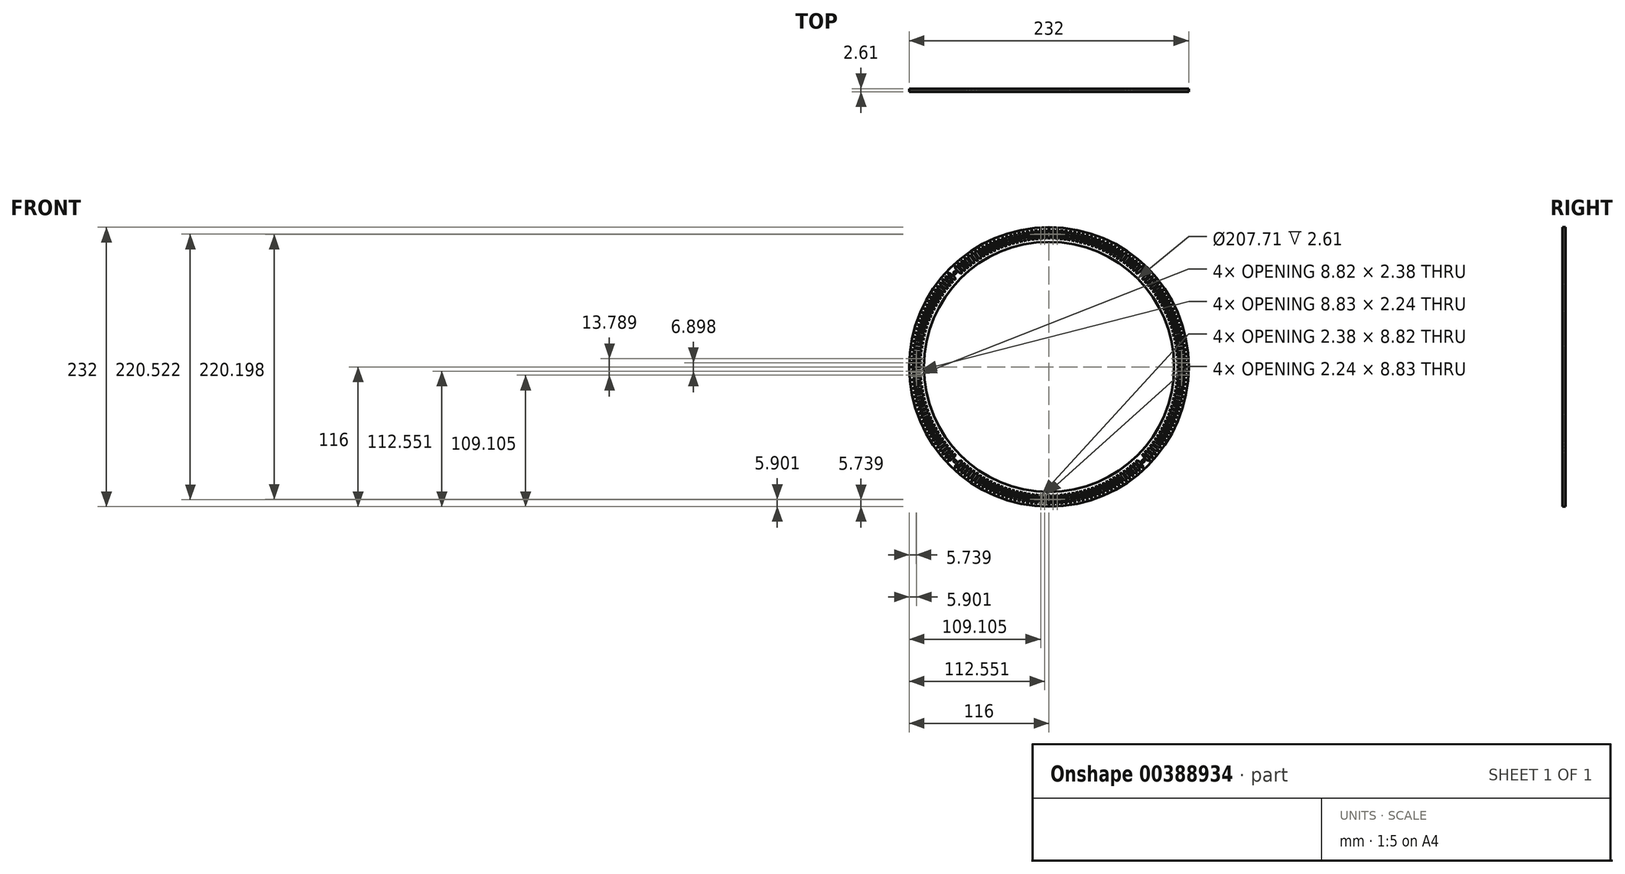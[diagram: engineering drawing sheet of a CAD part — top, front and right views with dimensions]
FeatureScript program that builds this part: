
annotation { "Feature Type Name" : "Feature", "Feature Type Description" : "" }
export const myFeature = defineFeature(function(context is Context, id is Id, definition is map)
    precondition{}
    {
        {
            var Q0;
            Q0=qCreatedBy(makeId("Front.planeOp"),FACE);
            var sketch = newSketch(context, id + "F0", { "sketchPlane" : qUnion([Q0])});
            skCircle(sketch, "E0", {"center": v(0, 0) * mm, "radius": 44.45 * mm});
            skCircle(sketch, "E1", {"center": v(0, 0) * mm, "radius": 39.8 * mm});
            skSolve(sketch);
        }
        {
            var Q0;
            Q0=makeQuery(id+"F0.imprint","IMPRINT",FACE,{"disambiguationData":[TD([[makeQuery(id+"F0.imprint","IMPRINT",EDGE,{"derivedFrom":sQuery(id+"F0.wireOp",EDGE,"E0")}),1.0]])]});
            extrude(context, id + "F1", {"entities" : qUnion([Q0]), "oppositeDirection" : true, "depth" : 1 * mm});
        }
        {
            var Q0;
            Q0=qCreatedBy(makeId("Front.planeOp"),FACE);
            var sketch = newSketch(context, id + "F2", { "sketchPlane" : qUnion([Q0])});
            skLineSegment(sketch, "E2", {"start": v(-43.11, 0.4) * mm, "end": v(-43.96, 0) * mm});
            skLineSegment(sketch, "E3", {"start": v(-41.42, 0.4) * mm, "end": v(-40.57, 0) * mm});
            skLineSegment(sketch, "E4", {"start": v(-40.57, 0) * mm, "end": v(-41.42, -0.4) * mm});
            skLineSegment(sketch, "E5", {"start": v(-43.96, 0) * mm, "end": v(-43.11, -0.4) * mm});
            skLineSegment(sketch, "E6", {"start": v(-43.11, 0.4) * mm, "end": v(-41.42, 0.4) * mm});
            skLineSegment(sketch, "E7", {"start": v(-41.42, -0.4) * mm, "end": v(-43.11, -0.4) * mm});
            skSolve(sketch);
        }
        {
            var Q0;
            Q0=qSketchRegion(id+"F2",true);
            extrude(context, id + "F3", {"entities" : qUnion([Q0]), "oppositeDirection" : true, "depth" : 1 * mm});
        }
        {
            var Q0;
            Q0=makeQuery(id+"F3.opExtrude","SWEPT_BODY",BODY,{"disambiguationData":[OSD([sQuery(id+"F2.wireOp",EDGE,"E2"),sQuery(id+"F2.wireOp",EDGE,"E3"),sQuery(id+"F2.wireOp",EDGE,"E4"),sQuery(id+"F2.wireOp",EDGE,"E5"),sQuery(id+"F2.wireOp",EDGE,"E6"),sQuery(id+"F2.wireOp",EDGE,"E7")])]});
            var Q1;
            Q1=sQuery(id+"F0.wireOp",EDGE,"E1");
            circularPattern(context, id + "F4", {"entities" : qUnion([Q0]), "axis" : qUnion([Q1]), "angle" : 43 * degree, "instanceCount" : 25, "equalSpace" : true});
        }
        {
            var Q0;
            Q0=makeQuery(id+"F3.opExtrude","SWEPT_BODY",BODY,{"disambiguationData":[OSD([sQuery(id+"F2.wireOp",EDGE,"E2"),sQuery(id+"F2.wireOp",EDGE,"E3"),sQuery(id+"F2.wireOp",EDGE,"E4"),sQuery(id+"F2.wireOp",EDGE,"E5"),sQuery(id+"F2.wireOp",EDGE,"E6"),sQuery(id+"F2.wireOp",EDGE,"E7")])]});
            var Q1;
            Q1=sQuery(id+"F0.wireOp",EDGE,"E1");
            circularPattern(context, id + "F5", {"entities" : qUnion([Q0]), "axis" : qUnion([Q1]), "angle" : 43 * degree, "instanceCount" : 25, "oppositeDirection" : true, "equalSpace" : true});
        }
        {
            var Q0;
            Q0=makeQuery(id+"F5.opPattern","COPY",BODY,{"derivedFrom":makeQuery(id+"F3.opExtrude","SWEPT_BODY",BODY,{"disambiguationData":[OSD([sQuery(id+"F2.wireOp",EDGE,"E2"),sQuery(id+"F2.wireOp",EDGE,"E3"),sQuery(id+"F2.wireOp",EDGE,"E4"),sQuery(id+"F2.wireOp",EDGE,"E5"),sQuery(id+"F2.wireOp",EDGE,"E6"),sQuery(id+"F2.wireOp",EDGE,"E7")])]}),"instanceName":"5"});
            var Q1;
            Q1=makeQuery(id+"F5.opPattern","COPY",BODY,{"derivedFrom":makeQuery(id+"F3.opExtrude","SWEPT_BODY",BODY,{"disambiguationData":[OSD([sQuery(id+"F2.wireOp",EDGE,"E2"),sQuery(id+"F2.wireOp",EDGE,"E3"),sQuery(id+"F2.wireOp",EDGE,"E4"),sQuery(id+"F2.wireOp",EDGE,"E5"),sQuery(id+"F2.wireOp",EDGE,"E6"),sQuery(id+"F2.wireOp",EDGE,"E7")])]}),"instanceName":"4"});
            var Q2;
            Q2=makeQuery(id+"F4.opPattern","COPY",BODY,{"derivedFrom":makeQuery(id+"F3.opExtrude","SWEPT_BODY",BODY,{"disambiguationData":[OSD([sQuery(id+"F2.wireOp",EDGE,"E2"),sQuery(id+"F2.wireOp",EDGE,"E3"),sQuery(id+"F2.wireOp",EDGE,"E4"),sQuery(id+"F2.wireOp",EDGE,"E5"),sQuery(id+"F2.wireOp",EDGE,"E6"),sQuery(id+"F2.wireOp",EDGE,"E7")])]}),"instanceName":"2"});
            var Q3;
            Q3=makeQuery(id+"F4.opPattern","COPY",BODY,{"derivedFrom":makeQuery(id+"F3.opExtrude","SWEPT_BODY",BODY,{"disambiguationData":[OSD([sQuery(id+"F2.wireOp",EDGE,"E2"),sQuery(id+"F2.wireOp",EDGE,"E3"),sQuery(id+"F2.wireOp",EDGE,"E4"),sQuery(id+"F2.wireOp",EDGE,"E5"),sQuery(id+"F2.wireOp",EDGE,"E6"),sQuery(id+"F2.wireOp",EDGE,"E7")])]}),"instanceName":"3"});
            var Q4;
            Q4=makeQuery(id+"F4.opPattern","COPY",BODY,{"derivedFrom":makeQuery(id+"F3.opExtrude","SWEPT_BODY",BODY,{"disambiguationData":[OSD([sQuery(id+"F2.wireOp",EDGE,"E2"),sQuery(id+"F2.wireOp",EDGE,"E3"),sQuery(id+"F2.wireOp",EDGE,"E4"),sQuery(id+"F2.wireOp",EDGE,"E5"),sQuery(id+"F2.wireOp",EDGE,"E6"),sQuery(id+"F2.wireOp",EDGE,"E7")])]}),"instanceName":"4"});
            var Q5;
            Q5=makeQuery(id+"F4.opPattern","COPY",BODY,{"derivedFrom":makeQuery(id+"F3.opExtrude","SWEPT_BODY",BODY,{"disambiguationData":[OSD([sQuery(id+"F2.wireOp",EDGE,"E2"),sQuery(id+"F2.wireOp",EDGE,"E3"),sQuery(id+"F2.wireOp",EDGE,"E4"),sQuery(id+"F2.wireOp",EDGE,"E5"),sQuery(id+"F2.wireOp",EDGE,"E6"),sQuery(id+"F2.wireOp",EDGE,"E7")])]}),"instanceName":"5"});
            var Q6;
            Q6=makeQuery(id+"F4.opPattern","COPY",BODY,{"derivedFrom":makeQuery(id+"F3.opExtrude","SWEPT_BODY",BODY,{"disambiguationData":[OSD([sQuery(id+"F2.wireOp",EDGE,"E2"),sQuery(id+"F2.wireOp",EDGE,"E3"),sQuery(id+"F2.wireOp",EDGE,"E4"),sQuery(id+"F2.wireOp",EDGE,"E5"),sQuery(id+"F2.wireOp",EDGE,"E6"),sQuery(id+"F2.wireOp",EDGE,"E7")])]}),"instanceName":"6"});
            var Q7;
            Q7=makeQuery(id+"F4.opPattern","COPY",BODY,{"derivedFrom":makeQuery(id+"F3.opExtrude","SWEPT_BODY",BODY,{"disambiguationData":[OSD([sQuery(id+"F2.wireOp",EDGE,"E2"),sQuery(id+"F2.wireOp",EDGE,"E3"),sQuery(id+"F2.wireOp",EDGE,"E4"),sQuery(id+"F2.wireOp",EDGE,"E5"),sQuery(id+"F2.wireOp",EDGE,"E6"),sQuery(id+"F2.wireOp",EDGE,"E7")])]}),"instanceName":"7"});
            var Q8;
            Q8=makeQuery(id+"F4.opPattern","COPY",BODY,{"derivedFrom":makeQuery(id+"F3.opExtrude","SWEPT_BODY",BODY,{"disambiguationData":[OSD([sQuery(id+"F2.wireOp",EDGE,"E2"),sQuery(id+"F2.wireOp",EDGE,"E3"),sQuery(id+"F2.wireOp",EDGE,"E4"),sQuery(id+"F2.wireOp",EDGE,"E5"),sQuery(id+"F2.wireOp",EDGE,"E6"),sQuery(id+"F2.wireOp",EDGE,"E7")])]}),"instanceName":"8"});
            var Q9;
            Q9=makeQuery(id+"F4.opPattern","COPY",BODY,{"derivedFrom":makeQuery(id+"F3.opExtrude","SWEPT_BODY",BODY,{"disambiguationData":[OSD([sQuery(id+"F2.wireOp",EDGE,"E2"),sQuery(id+"F2.wireOp",EDGE,"E3"),sQuery(id+"F2.wireOp",EDGE,"E4"),sQuery(id+"F2.wireOp",EDGE,"E5"),sQuery(id+"F2.wireOp",EDGE,"E6"),sQuery(id+"F2.wireOp",EDGE,"E7")])]}),"instanceName":"9"});
            var Q10;
            Q10=makeQuery(id+"F4.opPattern","COPY",BODY,{"derivedFrom":makeQuery(id+"F3.opExtrude","SWEPT_BODY",BODY,{"disambiguationData":[OSD([sQuery(id+"F2.wireOp",EDGE,"E2"),sQuery(id+"F2.wireOp",EDGE,"E3"),sQuery(id+"F2.wireOp",EDGE,"E4"),sQuery(id+"F2.wireOp",EDGE,"E5"),sQuery(id+"F2.wireOp",EDGE,"E6"),sQuery(id+"F2.wireOp",EDGE,"E7")])]}),"instanceName":"10"});
            var Q11;
            Q11=makeQuery(id+"F4.opPattern","COPY",BODY,{"derivedFrom":makeQuery(id+"F3.opExtrude","SWEPT_BODY",BODY,{"disambiguationData":[OSD([sQuery(id+"F2.wireOp",EDGE,"E2"),sQuery(id+"F2.wireOp",EDGE,"E3"),sQuery(id+"F2.wireOp",EDGE,"E4"),sQuery(id+"F2.wireOp",EDGE,"E5"),sQuery(id+"F2.wireOp",EDGE,"E6"),sQuery(id+"F2.wireOp",EDGE,"E7")])]}),"instanceName":"11"});
            var Q12;
            Q12=makeQuery(id+"F4.opPattern","COPY",BODY,{"derivedFrom":makeQuery(id+"F3.opExtrude","SWEPT_BODY",BODY,{"disambiguationData":[OSD([sQuery(id+"F2.wireOp",EDGE,"E2"),sQuery(id+"F2.wireOp",EDGE,"E3"),sQuery(id+"F2.wireOp",EDGE,"E4"),sQuery(id+"F2.wireOp",EDGE,"E5"),sQuery(id+"F2.wireOp",EDGE,"E6"),sQuery(id+"F2.wireOp",EDGE,"E7")])]}),"instanceName":"12"});
            var Q13;
            Q13=makeQuery(id+"F4.opPattern","COPY",BODY,{"derivedFrom":makeQuery(id+"F3.opExtrude","SWEPT_BODY",BODY,{"disambiguationData":[OSD([sQuery(id+"F2.wireOp",EDGE,"E2"),sQuery(id+"F2.wireOp",EDGE,"E3"),sQuery(id+"F2.wireOp",EDGE,"E4"),sQuery(id+"F2.wireOp",EDGE,"E5"),sQuery(id+"F2.wireOp",EDGE,"E6"),sQuery(id+"F2.wireOp",EDGE,"E7")])]}),"instanceName":"13"});
            var Q14;
            Q14=makeQuery(id+"F4.opPattern","COPY",BODY,{"derivedFrom":makeQuery(id+"F3.opExtrude","SWEPT_BODY",BODY,{"disambiguationData":[OSD([sQuery(id+"F2.wireOp",EDGE,"E2"),sQuery(id+"F2.wireOp",EDGE,"E3"),sQuery(id+"F2.wireOp",EDGE,"E4"),sQuery(id+"F2.wireOp",EDGE,"E5"),sQuery(id+"F2.wireOp",EDGE,"E6"),sQuery(id+"F2.wireOp",EDGE,"E7")])]}),"instanceName":"14"});
            var Q15;
            Q15=makeQuery(id+"F4.opPattern","COPY",BODY,{"derivedFrom":makeQuery(id+"F3.opExtrude","SWEPT_BODY",BODY,{"disambiguationData":[OSD([sQuery(id+"F2.wireOp",EDGE,"E2"),sQuery(id+"F2.wireOp",EDGE,"E3"),sQuery(id+"F2.wireOp",EDGE,"E4"),sQuery(id+"F2.wireOp",EDGE,"E5"),sQuery(id+"F2.wireOp",EDGE,"E6"),sQuery(id+"F2.wireOp",EDGE,"E7")])]}),"instanceName":"15"});
            var Q16;
            Q16=makeQuery(id+"F4.opPattern","COPY",BODY,{"derivedFrom":makeQuery(id+"F3.opExtrude","SWEPT_BODY",BODY,{"disambiguationData":[OSD([sQuery(id+"F2.wireOp",EDGE,"E2"),sQuery(id+"F2.wireOp",EDGE,"E3"),sQuery(id+"F2.wireOp",EDGE,"E4"),sQuery(id+"F2.wireOp",EDGE,"E5"),sQuery(id+"F2.wireOp",EDGE,"E6"),sQuery(id+"F2.wireOp",EDGE,"E7")])]}),"instanceName":"16"});
            var Q17;
            Q17=makeQuery(id+"F4.opPattern","COPY",BODY,{"derivedFrom":makeQuery(id+"F3.opExtrude","SWEPT_BODY",BODY,{"disambiguationData":[OSD([sQuery(id+"F2.wireOp",EDGE,"E2"),sQuery(id+"F2.wireOp",EDGE,"E3"),sQuery(id+"F2.wireOp",EDGE,"E4"),sQuery(id+"F2.wireOp",EDGE,"E5"),sQuery(id+"F2.wireOp",EDGE,"E6"),sQuery(id+"F2.wireOp",EDGE,"E7")])]}),"instanceName":"17"});
            var Q18;
            Q18=makeQuery(id+"F4.opPattern","COPY",BODY,{"derivedFrom":makeQuery(id+"F3.opExtrude","SWEPT_BODY",BODY,{"disambiguationData":[OSD([sQuery(id+"F2.wireOp",EDGE,"E2"),sQuery(id+"F2.wireOp",EDGE,"E3"),sQuery(id+"F2.wireOp",EDGE,"E4"),sQuery(id+"F2.wireOp",EDGE,"E5"),sQuery(id+"F2.wireOp",EDGE,"E6"),sQuery(id+"F2.wireOp",EDGE,"E7")])]}),"instanceName":"18"});
            var Q19;
            Q19=makeQuery(id+"F4.opPattern","COPY",BODY,{"derivedFrom":makeQuery(id+"F3.opExtrude","SWEPT_BODY",BODY,{"disambiguationData":[OSD([sQuery(id+"F2.wireOp",EDGE,"E2"),sQuery(id+"F2.wireOp",EDGE,"E3"),sQuery(id+"F2.wireOp",EDGE,"E4"),sQuery(id+"F2.wireOp",EDGE,"E5"),sQuery(id+"F2.wireOp",EDGE,"E6"),sQuery(id+"F2.wireOp",EDGE,"E7")])]}),"instanceName":"19"});
            var Q20;
            Q20=makeQuery(id+"F4.opPattern","COPY",BODY,{"derivedFrom":makeQuery(id+"F3.opExtrude","SWEPT_BODY",BODY,{"disambiguationData":[OSD([sQuery(id+"F2.wireOp",EDGE,"E2"),sQuery(id+"F2.wireOp",EDGE,"E3"),sQuery(id+"F2.wireOp",EDGE,"E4"),sQuery(id+"F2.wireOp",EDGE,"E5"),sQuery(id+"F2.wireOp",EDGE,"E6"),sQuery(id+"F2.wireOp",EDGE,"E7")])]}),"instanceName":"20"});
            var Q21;
            Q21=makeQuery(id+"F5.opPattern","COPY",BODY,{"derivedFrom":makeQuery(id+"F3.opExtrude","SWEPT_BODY",BODY,{"disambiguationData":[OSD([sQuery(id+"F2.wireOp",EDGE,"E2"),sQuery(id+"F2.wireOp",EDGE,"E3"),sQuery(id+"F2.wireOp",EDGE,"E4"),sQuery(id+"F2.wireOp",EDGE,"E5"),sQuery(id+"F2.wireOp",EDGE,"E6"),sQuery(id+"F2.wireOp",EDGE,"E7")])]}),"instanceName":"24"});
            var Q22;
            Q22=makeQuery(id+"F5.opPattern","COPY",BODY,{"derivedFrom":makeQuery(id+"F3.opExtrude","SWEPT_BODY",BODY,{"disambiguationData":[OSD([sQuery(id+"F2.wireOp",EDGE,"E2"),sQuery(id+"F2.wireOp",EDGE,"E3"),sQuery(id+"F2.wireOp",EDGE,"E4"),sQuery(id+"F2.wireOp",EDGE,"E5"),sQuery(id+"F2.wireOp",EDGE,"E6"),sQuery(id+"F2.wireOp",EDGE,"E7")])]}),"instanceName":"23"});
            var Q23;
            Q23=makeQuery(id+"F5.opPattern","COPY",BODY,{"derivedFrom":makeQuery(id+"F3.opExtrude","SWEPT_BODY",BODY,{"disambiguationData":[OSD([sQuery(id+"F2.wireOp",EDGE,"E2"),sQuery(id+"F2.wireOp",EDGE,"E3"),sQuery(id+"F2.wireOp",EDGE,"E4"),sQuery(id+"F2.wireOp",EDGE,"E5"),sQuery(id+"F2.wireOp",EDGE,"E6"),sQuery(id+"F2.wireOp",EDGE,"E7")])]}),"instanceName":"22"});
            var Q24;
            Q24=makeQuery(id+"F5.opPattern","COPY",BODY,{"derivedFrom":makeQuery(id+"F3.opExtrude","SWEPT_BODY",BODY,{"disambiguationData":[OSD([sQuery(id+"F2.wireOp",EDGE,"E2"),sQuery(id+"F2.wireOp",EDGE,"E3"),sQuery(id+"F2.wireOp",EDGE,"E4"),sQuery(id+"F2.wireOp",EDGE,"E5"),sQuery(id+"F2.wireOp",EDGE,"E6"),sQuery(id+"F2.wireOp",EDGE,"E7")])]}),"instanceName":"21"});
            var Q25;
            Q25=makeQuery(id+"F5.opPattern","COPY",BODY,{"derivedFrom":makeQuery(id+"F3.opExtrude","SWEPT_BODY",BODY,{"disambiguationData":[OSD([sQuery(id+"F2.wireOp",EDGE,"E2"),sQuery(id+"F2.wireOp",EDGE,"E3"),sQuery(id+"F2.wireOp",EDGE,"E4"),sQuery(id+"F2.wireOp",EDGE,"E5"),sQuery(id+"F2.wireOp",EDGE,"E6"),sQuery(id+"F2.wireOp",EDGE,"E7")])]}),"instanceName":"20"});
            var Q26;
            Q26=makeQuery(id+"F5.opPattern","COPY",BODY,{"derivedFrom":makeQuery(id+"F3.opExtrude","SWEPT_BODY",BODY,{"disambiguationData":[OSD([sQuery(id+"F2.wireOp",EDGE,"E2"),sQuery(id+"F2.wireOp",EDGE,"E3"),sQuery(id+"F2.wireOp",EDGE,"E4"),sQuery(id+"F2.wireOp",EDGE,"E5"),sQuery(id+"F2.wireOp",EDGE,"E6"),sQuery(id+"F2.wireOp",EDGE,"E7")])]}),"instanceName":"19"});
            var Q27;
            Q27=makeQuery(id+"F5.opPattern","COPY",BODY,{"derivedFrom":makeQuery(id+"F3.opExtrude","SWEPT_BODY",BODY,{"disambiguationData":[OSD([sQuery(id+"F2.wireOp",EDGE,"E2"),sQuery(id+"F2.wireOp",EDGE,"E3"),sQuery(id+"F2.wireOp",EDGE,"E4"),sQuery(id+"F2.wireOp",EDGE,"E5"),sQuery(id+"F2.wireOp",EDGE,"E6"),sQuery(id+"F2.wireOp",EDGE,"E7")])]}),"instanceName":"18"});
            var Q28;
            Q28=makeQuery(id+"F5.opPattern","COPY",BODY,{"derivedFrom":makeQuery(id+"F3.opExtrude","SWEPT_BODY",BODY,{"disambiguationData":[OSD([sQuery(id+"F2.wireOp",EDGE,"E2"),sQuery(id+"F2.wireOp",EDGE,"E3"),sQuery(id+"F2.wireOp",EDGE,"E4"),sQuery(id+"F2.wireOp",EDGE,"E5"),sQuery(id+"F2.wireOp",EDGE,"E6"),sQuery(id+"F2.wireOp",EDGE,"E7")])]}),"instanceName":"17"});
            var Q29;
            Q29=makeQuery(id+"F5.opPattern","COPY",BODY,{"derivedFrom":makeQuery(id+"F3.opExtrude","SWEPT_BODY",BODY,{"disambiguationData":[OSD([sQuery(id+"F2.wireOp",EDGE,"E2"),sQuery(id+"F2.wireOp",EDGE,"E3"),sQuery(id+"F2.wireOp",EDGE,"E4"),sQuery(id+"F2.wireOp",EDGE,"E5"),sQuery(id+"F2.wireOp",EDGE,"E6"),sQuery(id+"F2.wireOp",EDGE,"E7")])]}),"instanceName":"16"});
            var Q30;
            Q30=makeQuery(id+"F5.opPattern","COPY",BODY,{"derivedFrom":makeQuery(id+"F3.opExtrude","SWEPT_BODY",BODY,{"disambiguationData":[OSD([sQuery(id+"F2.wireOp",EDGE,"E2"),sQuery(id+"F2.wireOp",EDGE,"E3"),sQuery(id+"F2.wireOp",EDGE,"E4"),sQuery(id+"F2.wireOp",EDGE,"E5"),sQuery(id+"F2.wireOp",EDGE,"E6"),sQuery(id+"F2.wireOp",EDGE,"E7")])]}),"instanceName":"15"});
            var Q31;
            Q31=makeQuery(id+"F5.opPattern","COPY",BODY,{"derivedFrom":makeQuery(id+"F3.opExtrude","SWEPT_BODY",BODY,{"disambiguationData":[OSD([sQuery(id+"F2.wireOp",EDGE,"E2"),sQuery(id+"F2.wireOp",EDGE,"E3"),sQuery(id+"F2.wireOp",EDGE,"E4"),sQuery(id+"F2.wireOp",EDGE,"E5"),sQuery(id+"F2.wireOp",EDGE,"E6"),sQuery(id+"F2.wireOp",EDGE,"E7")])]}),"instanceName":"14"});
            var Q32;
            Q32=makeQuery(id+"F5.opPattern","COPY",BODY,{"derivedFrom":makeQuery(id+"F3.opExtrude","SWEPT_BODY",BODY,{"disambiguationData":[OSD([sQuery(id+"F2.wireOp",EDGE,"E2"),sQuery(id+"F2.wireOp",EDGE,"E3"),sQuery(id+"F2.wireOp",EDGE,"E4"),sQuery(id+"F2.wireOp",EDGE,"E5"),sQuery(id+"F2.wireOp",EDGE,"E6"),sQuery(id+"F2.wireOp",EDGE,"E7")])]}),"instanceName":"13"});
            var Q33;
            Q33=makeQuery(id+"F5.opPattern","COPY",BODY,{"derivedFrom":makeQuery(id+"F3.opExtrude","SWEPT_BODY",BODY,{"disambiguationData":[OSD([sQuery(id+"F2.wireOp",EDGE,"E2"),sQuery(id+"F2.wireOp",EDGE,"E3"),sQuery(id+"F2.wireOp",EDGE,"E4"),sQuery(id+"F2.wireOp",EDGE,"E5"),sQuery(id+"F2.wireOp",EDGE,"E6"),sQuery(id+"F2.wireOp",EDGE,"E7")])]}),"instanceName":"12"});
            var Q34;
            Q34=makeQuery(id+"F5.opPattern","COPY",BODY,{"derivedFrom":makeQuery(id+"F3.opExtrude","SWEPT_BODY",BODY,{"disambiguationData":[OSD([sQuery(id+"F2.wireOp",EDGE,"E2"),sQuery(id+"F2.wireOp",EDGE,"E3"),sQuery(id+"F2.wireOp",EDGE,"E4"),sQuery(id+"F2.wireOp",EDGE,"E5"),sQuery(id+"F2.wireOp",EDGE,"E6"),sQuery(id+"F2.wireOp",EDGE,"E7")])]}),"instanceName":"11"});
            var Q35;
            Q35=makeQuery(id+"F5.opPattern","COPY",BODY,{"derivedFrom":makeQuery(id+"F3.opExtrude","SWEPT_BODY",BODY,{"disambiguationData":[OSD([sQuery(id+"F2.wireOp",EDGE,"E2"),sQuery(id+"F2.wireOp",EDGE,"E3"),sQuery(id+"F2.wireOp",EDGE,"E4"),sQuery(id+"F2.wireOp",EDGE,"E5"),sQuery(id+"F2.wireOp",EDGE,"E6"),sQuery(id+"F2.wireOp",EDGE,"E7")])]}),"instanceName":"10"});
            var Q36;
            Q36=makeQuery(id+"F5.opPattern","COPY",BODY,{"derivedFrom":makeQuery(id+"F3.opExtrude","SWEPT_BODY",BODY,{"disambiguationData":[OSD([sQuery(id+"F2.wireOp",EDGE,"E2"),sQuery(id+"F2.wireOp",EDGE,"E3"),sQuery(id+"F2.wireOp",EDGE,"E4"),sQuery(id+"F2.wireOp",EDGE,"E5"),sQuery(id+"F2.wireOp",EDGE,"E6"),sQuery(id+"F2.wireOp",EDGE,"E7")])]}),"instanceName":"9"});
            var Q37;
            Q37=makeQuery(id+"F5.opPattern","COPY",BODY,{"derivedFrom":makeQuery(id+"F3.opExtrude","SWEPT_BODY",BODY,{"disambiguationData":[OSD([sQuery(id+"F2.wireOp",EDGE,"E2"),sQuery(id+"F2.wireOp",EDGE,"E3"),sQuery(id+"F2.wireOp",EDGE,"E4"),sQuery(id+"F2.wireOp",EDGE,"E5"),sQuery(id+"F2.wireOp",EDGE,"E6"),sQuery(id+"F2.wireOp",EDGE,"E7")])]}),"instanceName":"8"});
            var Q38;
            Q38=makeQuery(id+"F5.opPattern","COPY",BODY,{"derivedFrom":makeQuery(id+"F3.opExtrude","SWEPT_BODY",BODY,{"disambiguationData":[OSD([sQuery(id+"F2.wireOp",EDGE,"E2"),sQuery(id+"F2.wireOp",EDGE,"E3"),sQuery(id+"F2.wireOp",EDGE,"E4"),sQuery(id+"F2.wireOp",EDGE,"E5"),sQuery(id+"F2.wireOp",EDGE,"E6"),sQuery(id+"F2.wireOp",EDGE,"E7")])]}),"instanceName":"7"});
            var Q39;
            Q39=makeQuery(id+"F5.opPattern","COPY",BODY,{"derivedFrom":makeQuery(id+"F3.opExtrude","SWEPT_BODY",BODY,{"disambiguationData":[OSD([sQuery(id+"F2.wireOp",EDGE,"E2"),sQuery(id+"F2.wireOp",EDGE,"E3"),sQuery(id+"F2.wireOp",EDGE,"E4"),sQuery(id+"F2.wireOp",EDGE,"E5"),sQuery(id+"F2.wireOp",EDGE,"E6"),sQuery(id+"F2.wireOp",EDGE,"E7")])]}),"instanceName":"6"});
            var Q40;
            Q40=makeQuery(id+"F5.opPattern","COPY",BODY,{"derivedFrom":makeQuery(id+"F3.opExtrude","SWEPT_BODY",BODY,{"disambiguationData":[OSD([sQuery(id+"F2.wireOp",EDGE,"E2"),sQuery(id+"F2.wireOp",EDGE,"E3"),sQuery(id+"F2.wireOp",EDGE,"E4"),sQuery(id+"F2.wireOp",EDGE,"E5"),sQuery(id+"F2.wireOp",EDGE,"E6"),sQuery(id+"F2.wireOp",EDGE,"E7")])]}),"instanceName":"2"});
            var Q41;
            Q41=makeQuery(id+"F5.opPattern","COPY",BODY,{"derivedFrom":makeQuery(id+"F3.opExtrude","SWEPT_BODY",BODY,{"disambiguationData":[OSD([sQuery(id+"F2.wireOp",EDGE,"E2"),sQuery(id+"F2.wireOp",EDGE,"E3"),sQuery(id+"F2.wireOp",EDGE,"E4"),sQuery(id+"F2.wireOp",EDGE,"E5"),sQuery(id+"F2.wireOp",EDGE,"E6"),sQuery(id+"F2.wireOp",EDGE,"E7")])]}),"instanceName":"3"});
            var Q42;
            Q42=makeQuery(id+"F3.opExtrude","SWEPT_BODY",BODY,{"disambiguationData":[OSD([sQuery(id+"F2.wireOp",EDGE,"E2"),sQuery(id+"F2.wireOp",EDGE,"E3"),sQuery(id+"F2.wireOp",EDGE,"E4"),sQuery(id+"F2.wireOp",EDGE,"E5"),sQuery(id+"F2.wireOp",EDGE,"E6"),sQuery(id+"F2.wireOp",EDGE,"E7")])]});
            var Q43;
            Q43=makeQuery(id+"F4.opPattern","COPY",BODY,{"derivedFrom":makeQuery(id+"F3.opExtrude","SWEPT_BODY",BODY,{"disambiguationData":[OSD([sQuery(id+"F2.wireOp",EDGE,"E2"),sQuery(id+"F2.wireOp",EDGE,"E3"),sQuery(id+"F2.wireOp",EDGE,"E4"),sQuery(id+"F2.wireOp",EDGE,"E5"),sQuery(id+"F2.wireOp",EDGE,"E6"),sQuery(id+"F2.wireOp",EDGE,"E7")])]}),"instanceName":"1"});
            var Q44;
            Q44=makeQuery(id+"F5.opPattern","COPY",BODY,{"derivedFrom":makeQuery(id+"F3.opExtrude","SWEPT_BODY",BODY,{"disambiguationData":[OSD([sQuery(id+"F2.wireOp",EDGE,"E2"),sQuery(id+"F2.wireOp",EDGE,"E3"),sQuery(id+"F2.wireOp",EDGE,"E4"),sQuery(id+"F2.wireOp",EDGE,"E5"),sQuery(id+"F2.wireOp",EDGE,"E6"),sQuery(id+"F2.wireOp",EDGE,"E7")])]}),"instanceName":"1"});
            var Q45;
            Q45=makeQuery(id+"F4.opPattern","COPY",BODY,{"derivedFrom":makeQuery(id+"F3.opExtrude","SWEPT_BODY",BODY,{"disambiguationData":[OSD([sQuery(id+"F2.wireOp",EDGE,"E2"),sQuery(id+"F2.wireOp",EDGE,"E3"),sQuery(id+"F2.wireOp",EDGE,"E4"),sQuery(id+"F2.wireOp",EDGE,"E5"),sQuery(id+"F2.wireOp",EDGE,"E6"),sQuery(id+"F2.wireOp",EDGE,"E7")])]}),"instanceName":"21"});
            var Q46;
            Q46=makeQuery(id+"F4.opPattern","COPY",BODY,{"derivedFrom":makeQuery(id+"F3.opExtrude","SWEPT_BODY",BODY,{"disambiguationData":[OSD([sQuery(id+"F2.wireOp",EDGE,"E2"),sQuery(id+"F2.wireOp",EDGE,"E3"),sQuery(id+"F2.wireOp",EDGE,"E4"),sQuery(id+"F2.wireOp",EDGE,"E5"),sQuery(id+"F2.wireOp",EDGE,"E6"),sQuery(id+"F2.wireOp",EDGE,"E7")])]}),"instanceName":"22"});
            var Q47;
            Q47=makeQuery(id+"F4.opPattern","COPY",BODY,{"derivedFrom":makeQuery(id+"F3.opExtrude","SWEPT_BODY",BODY,{"disambiguationData":[OSD([sQuery(id+"F2.wireOp",EDGE,"E2"),sQuery(id+"F2.wireOp",EDGE,"E3"),sQuery(id+"F2.wireOp",EDGE,"E4"),sQuery(id+"F2.wireOp",EDGE,"E5"),sQuery(id+"F2.wireOp",EDGE,"E6"),sQuery(id+"F2.wireOp",EDGE,"E7")])]}),"instanceName":"23"});
            var Q48;
            Q48=makeQuery(id+"F4.opPattern","COPY",BODY,{"derivedFrom":makeQuery(id+"F3.opExtrude","SWEPT_BODY",BODY,{"disambiguationData":[OSD([sQuery(id+"F2.wireOp",EDGE,"E2"),sQuery(id+"F2.wireOp",EDGE,"E3"),sQuery(id+"F2.wireOp",EDGE,"E4"),sQuery(id+"F2.wireOp",EDGE,"E5"),sQuery(id+"F2.wireOp",EDGE,"E6"),sQuery(id+"F2.wireOp",EDGE,"E7")])]}),"instanceName":"24"});
            var Q49;
            Q49=sQuery(id+"F0.wireOp",EDGE,"E1");
            circularPattern(context, id + "F6", {"entities" : qUnion([Q0, Q1, Q2, Q3, Q4, Q5, Q6, Q7, Q8, Q9, Q10, Q11, Q12, Q13, Q14, Q15, Q16, Q17, Q18, Q19, Q20, Q21, Q22, Q23, Q24, Q25, Q26, Q27, Q28, Q29, Q30, Q31, Q32, Q33, Q34, Q35, Q36, Q37, Q38, Q39, Q40, Q41, Q42, Q43, Q44, Q45, Q46, Q47, Q48]), "axis" : qUnion([Q49]), "angle" : 360 * degree, "instanceCount" : 4, "equalSpace" : true});
        }
        {
            var Q0;
            Q0=makeQuery(id+"F0.imprint","IMPRINT",FACE,{"disambiguationData":[TD([[makeQuery(id+"F0.imprint","IMPRINT",EDGE,{"derivedFrom":sQuery(id+"F0.wireOp",EDGE,"E0")}),1.0]])]});
            var sketch = newSketch(context, id + "F7", { "sketchPlane" : qUnion([Q0])});
            skCircle(sketch, "E8", {"center": v(-29.95, -29.95) * mm, "radius": 0.45 * mm});
            skCircle(sketch, "E9.1.0", {"center": v(29.95, -29.95) * mm, "radius": 0.45 * mm});
            skCircle(sketch, "E9.2.0", {"center": v(29.95, 29.95) * mm, "radius": 0.45 * mm});
            skCircle(sketch, "E9.3.0", {"center": v(-29.95, 29.95) * mm, "radius": 0.45 * mm});
            skPoint(sketch, "E9.center", {"position": v(0, 0) * mm});
            skSolve(sketch);
        }
        {
            var Q0;
            Q0=qSketchRegion(id+"F7",true);
            extrude(context, id + "F8", {"entities" : qUnion([Q0]), "oppositeDirection" : true, "depth" : 1 * mm});
        }
        {
            var Q0;
            Q0=makeQuery(id+"F5.opPattern","COPY",BODY,{"derivedFrom":makeQuery(id+"F3.opExtrude","SWEPT_BODY",BODY,{"disambiguationData":[OSD([sQuery(id+"F2.wireOp",EDGE,"E2"),sQuery(id+"F2.wireOp",EDGE,"E3"),sQuery(id+"F2.wireOp",EDGE,"E4"),sQuery(id+"F2.wireOp",EDGE,"E5"),sQuery(id+"F2.wireOp",EDGE,"E6"),sQuery(id+"F2.wireOp",EDGE,"E7")])]}),"instanceName":"9"});
            var Q1;
            Q1=makeQuery(id+"F5.opPattern","COPY",BODY,{"derivedFrom":makeQuery(id+"F3.opExtrude","SWEPT_BODY",BODY,{"disambiguationData":[OSD([sQuery(id+"F2.wireOp",EDGE,"E2"),sQuery(id+"F2.wireOp",EDGE,"E3"),sQuery(id+"F2.wireOp",EDGE,"E4"),sQuery(id+"F2.wireOp",EDGE,"E5"),sQuery(id+"F2.wireOp",EDGE,"E6"),sQuery(id+"F2.wireOp",EDGE,"E7")])]}),"instanceName":"8"});
            var Q2;
            Q2=makeQuery(id+"F5.opPattern","COPY",BODY,{"derivedFrom":makeQuery(id+"F3.opExtrude","SWEPT_BODY",BODY,{"disambiguationData":[OSD([sQuery(id+"F2.wireOp",EDGE,"E2"),sQuery(id+"F2.wireOp",EDGE,"E3"),sQuery(id+"F2.wireOp",EDGE,"E4"),sQuery(id+"F2.wireOp",EDGE,"E5"),sQuery(id+"F2.wireOp",EDGE,"E6"),sQuery(id+"F2.wireOp",EDGE,"E7")])]}),"instanceName":"4"});
            var Q3;
            Q3=makeQuery(id+"F6.opPattern","COPY",BODY,{"derivedFrom":makeQuery(id+"F5.opPattern","COPY",BODY,{"derivedFrom":makeQuery(id+"F3.opExtrude","SWEPT_BODY",BODY,{"disambiguationData":[OSD([sQuery(id+"F2.wireOp",EDGE,"E2"),sQuery(id+"F2.wireOp",EDGE,"E3"),sQuery(id+"F2.wireOp",EDGE,"E4"),sQuery(id+"F2.wireOp",EDGE,"E5"),sQuery(id+"F2.wireOp",EDGE,"E6"),sQuery(id+"F2.wireOp",EDGE,"E7")])]}),"instanceName":"1"}),"instanceName":"3"});
            var Q4;
            Q4=makeQuery(id+"F6.opPattern","COPY",BODY,{"derivedFrom":makeQuery(id+"F5.opPattern","COPY",BODY,{"derivedFrom":makeQuery(id+"F3.opExtrude","SWEPT_BODY",BODY,{"disambiguationData":[OSD([sQuery(id+"F2.wireOp",EDGE,"E2"),sQuery(id+"F2.wireOp",EDGE,"E3"),sQuery(id+"F2.wireOp",EDGE,"E4"),sQuery(id+"F2.wireOp",EDGE,"E5"),sQuery(id+"F2.wireOp",EDGE,"E6"),sQuery(id+"F2.wireOp",EDGE,"E7")])]}),"instanceName":"23"}),"instanceName":"3"});
            var Q5;
            Q5=makeQuery(id+"F6.opPattern","COPY",BODY,{"derivedFrom":makeQuery(id+"F5.opPattern","COPY",BODY,{"derivedFrom":makeQuery(id+"F3.opExtrude","SWEPT_BODY",BODY,{"disambiguationData":[OSD([sQuery(id+"F2.wireOp",EDGE,"E2"),sQuery(id+"F2.wireOp",EDGE,"E3"),sQuery(id+"F2.wireOp",EDGE,"E4"),sQuery(id+"F2.wireOp",EDGE,"E5"),sQuery(id+"F2.wireOp",EDGE,"E6"),sQuery(id+"F2.wireOp",EDGE,"E7")])]}),"instanceName":"22"}),"instanceName":"3"});
            var Q6;
            Q6=makeQuery(id+"F6.opPattern","COPY",BODY,{"derivedFrom":makeQuery(id+"F5.opPattern","COPY",BODY,{"derivedFrom":makeQuery(id+"F3.opExtrude","SWEPT_BODY",BODY,{"disambiguationData":[OSD([sQuery(id+"F2.wireOp",EDGE,"E2"),sQuery(id+"F2.wireOp",EDGE,"E3"),sQuery(id+"F2.wireOp",EDGE,"E4"),sQuery(id+"F2.wireOp",EDGE,"E5"),sQuery(id+"F2.wireOp",EDGE,"E6"),sQuery(id+"F2.wireOp",EDGE,"E7")])]}),"instanceName":"21"}),"instanceName":"3"});
            var Q7;
            Q7=makeQuery(id+"F6.opPattern","COPY",BODY,{"derivedFrom":makeQuery(id+"F5.opPattern","COPY",BODY,{"derivedFrom":makeQuery(id+"F3.opExtrude","SWEPT_BODY",BODY,{"disambiguationData":[OSD([sQuery(id+"F2.wireOp",EDGE,"E2"),sQuery(id+"F2.wireOp",EDGE,"E3"),sQuery(id+"F2.wireOp",EDGE,"E4"),sQuery(id+"F2.wireOp",EDGE,"E5"),sQuery(id+"F2.wireOp",EDGE,"E6"),sQuery(id+"F2.wireOp",EDGE,"E7")])]}),"instanceName":"20"}),"instanceName":"3"});
            var Q8;
            Q8=makeQuery(id+"F6.opPattern","COPY",BODY,{"derivedFrom":makeQuery(id+"F5.opPattern","COPY",BODY,{"derivedFrom":makeQuery(id+"F3.opExtrude","SWEPT_BODY",BODY,{"disambiguationData":[OSD([sQuery(id+"F2.wireOp",EDGE,"E2"),sQuery(id+"F2.wireOp",EDGE,"E3"),sQuery(id+"F2.wireOp",EDGE,"E4"),sQuery(id+"F2.wireOp",EDGE,"E5"),sQuery(id+"F2.wireOp",EDGE,"E6"),sQuery(id+"F2.wireOp",EDGE,"E7")])]}),"instanceName":"19"}),"instanceName":"3"});
            var Q9;
            Q9=makeQuery(id+"F6.opPattern","COPY",BODY,{"derivedFrom":makeQuery(id+"F5.opPattern","COPY",BODY,{"derivedFrom":makeQuery(id+"F3.opExtrude","SWEPT_BODY",BODY,{"disambiguationData":[OSD([sQuery(id+"F2.wireOp",EDGE,"E2"),sQuery(id+"F2.wireOp",EDGE,"E3"),sQuery(id+"F2.wireOp",EDGE,"E4"),sQuery(id+"F2.wireOp",EDGE,"E5"),sQuery(id+"F2.wireOp",EDGE,"E6"),sQuery(id+"F2.wireOp",EDGE,"E7")])]}),"instanceName":"18"}),"instanceName":"3"});
            var Q10;
            Q10=makeQuery(id+"F6.opPattern","COPY",BODY,{"derivedFrom":makeQuery(id+"F5.opPattern","COPY",BODY,{"derivedFrom":makeQuery(id+"F3.opExtrude","SWEPT_BODY",BODY,{"disambiguationData":[OSD([sQuery(id+"F2.wireOp",EDGE,"E2"),sQuery(id+"F2.wireOp",EDGE,"E3"),sQuery(id+"F2.wireOp",EDGE,"E4"),sQuery(id+"F2.wireOp",EDGE,"E5"),sQuery(id+"F2.wireOp",EDGE,"E6"),sQuery(id+"F2.wireOp",EDGE,"E7")])]}),"instanceName":"17"}),"instanceName":"3"});
            var Q11;
            Q11=makeQuery(id+"F6.opPattern","COPY",BODY,{"derivedFrom":makeQuery(id+"F5.opPattern","COPY",BODY,{"derivedFrom":makeQuery(id+"F3.opExtrude","SWEPT_BODY",BODY,{"disambiguationData":[OSD([sQuery(id+"F2.wireOp",EDGE,"E2"),sQuery(id+"F2.wireOp",EDGE,"E3"),sQuery(id+"F2.wireOp",EDGE,"E4"),sQuery(id+"F2.wireOp",EDGE,"E5"),sQuery(id+"F2.wireOp",EDGE,"E6"),sQuery(id+"F2.wireOp",EDGE,"E7")])]}),"instanceName":"16"}),"instanceName":"3"});
            var Q12;
            Q12=makeQuery(id+"F6.opPattern","COPY",BODY,{"derivedFrom":makeQuery(id+"F5.opPattern","COPY",BODY,{"derivedFrom":makeQuery(id+"F3.opExtrude","SWEPT_BODY",BODY,{"disambiguationData":[OSD([sQuery(id+"F2.wireOp",EDGE,"E2"),sQuery(id+"F2.wireOp",EDGE,"E3"),sQuery(id+"F2.wireOp",EDGE,"E4"),sQuery(id+"F2.wireOp",EDGE,"E5"),sQuery(id+"F2.wireOp",EDGE,"E6"),sQuery(id+"F2.wireOp",EDGE,"E7")])]}),"instanceName":"15"}),"instanceName":"3"});
            var Q13;
            Q13=makeQuery(id+"F6.opPattern","COPY",BODY,{"derivedFrom":makeQuery(id+"F5.opPattern","COPY",BODY,{"derivedFrom":makeQuery(id+"F3.opExtrude","SWEPT_BODY",BODY,{"disambiguationData":[OSD([sQuery(id+"F2.wireOp",EDGE,"E2"),sQuery(id+"F2.wireOp",EDGE,"E3"),sQuery(id+"F2.wireOp",EDGE,"E4"),sQuery(id+"F2.wireOp",EDGE,"E5"),sQuery(id+"F2.wireOp",EDGE,"E6"),sQuery(id+"F2.wireOp",EDGE,"E7")])]}),"instanceName":"14"}),"instanceName":"3"});
            var Q14;
            Q14=makeQuery(id+"F6.opPattern","COPY",BODY,{"derivedFrom":makeQuery(id+"F5.opPattern","COPY",BODY,{"derivedFrom":makeQuery(id+"F3.opExtrude","SWEPT_BODY",BODY,{"disambiguationData":[OSD([sQuery(id+"F2.wireOp",EDGE,"E2"),sQuery(id+"F2.wireOp",EDGE,"E3"),sQuery(id+"F2.wireOp",EDGE,"E4"),sQuery(id+"F2.wireOp",EDGE,"E5"),sQuery(id+"F2.wireOp",EDGE,"E6"),sQuery(id+"F2.wireOp",EDGE,"E7")])]}),"instanceName":"13"}),"instanceName":"3"});
            var Q15;
            Q15=makeQuery(id+"F6.opPattern","COPY",BODY,{"derivedFrom":makeQuery(id+"F5.opPattern","COPY",BODY,{"derivedFrom":makeQuery(id+"F3.opExtrude","SWEPT_BODY",BODY,{"disambiguationData":[OSD([sQuery(id+"F2.wireOp",EDGE,"E2"),sQuery(id+"F2.wireOp",EDGE,"E3"),sQuery(id+"F2.wireOp",EDGE,"E4"),sQuery(id+"F2.wireOp",EDGE,"E5"),sQuery(id+"F2.wireOp",EDGE,"E6"),sQuery(id+"F2.wireOp",EDGE,"E7")])]}),"instanceName":"12"}),"instanceName":"3"});
            var Q16;
            Q16=makeQuery(id+"F6.opPattern","COPY",BODY,{"derivedFrom":makeQuery(id+"F5.opPattern","COPY",BODY,{"derivedFrom":makeQuery(id+"F3.opExtrude","SWEPT_BODY",BODY,{"disambiguationData":[OSD([sQuery(id+"F2.wireOp",EDGE,"E2"),sQuery(id+"F2.wireOp",EDGE,"E3"),sQuery(id+"F2.wireOp",EDGE,"E4"),sQuery(id+"F2.wireOp",EDGE,"E5"),sQuery(id+"F2.wireOp",EDGE,"E6"),sQuery(id+"F2.wireOp",EDGE,"E7")])]}),"instanceName":"11"}),"instanceName":"3"});
            var Q17;
            Q17=makeQuery(id+"F6.opPattern","COPY",BODY,{"derivedFrom":makeQuery(id+"F5.opPattern","COPY",BODY,{"derivedFrom":makeQuery(id+"F3.opExtrude","SWEPT_BODY",BODY,{"disambiguationData":[OSD([sQuery(id+"F2.wireOp",EDGE,"E2"),sQuery(id+"F2.wireOp",EDGE,"E3"),sQuery(id+"F2.wireOp",EDGE,"E4"),sQuery(id+"F2.wireOp",EDGE,"E5"),sQuery(id+"F2.wireOp",EDGE,"E6"),sQuery(id+"F2.wireOp",EDGE,"E7")])]}),"instanceName":"10"}),"instanceName":"3"});
            var Q18;
            Q18=makeQuery(id+"F6.opPattern","COPY",BODY,{"derivedFrom":makeQuery(id+"F5.opPattern","COPY",BODY,{"derivedFrom":makeQuery(id+"F3.opExtrude","SWEPT_BODY",BODY,{"disambiguationData":[OSD([sQuery(id+"F2.wireOp",EDGE,"E2"),sQuery(id+"F2.wireOp",EDGE,"E3"),sQuery(id+"F2.wireOp",EDGE,"E4"),sQuery(id+"F2.wireOp",EDGE,"E5"),sQuery(id+"F2.wireOp",EDGE,"E6"),sQuery(id+"F2.wireOp",EDGE,"E7")])]}),"instanceName":"9"}),"instanceName":"3"});
            var Q19;
            Q19=makeQuery(id+"F6.opPattern","COPY",BODY,{"derivedFrom":makeQuery(id+"F5.opPattern","COPY",BODY,{"derivedFrom":makeQuery(id+"F3.opExtrude","SWEPT_BODY",BODY,{"disambiguationData":[OSD([sQuery(id+"F2.wireOp",EDGE,"E2"),sQuery(id+"F2.wireOp",EDGE,"E3"),sQuery(id+"F2.wireOp",EDGE,"E4"),sQuery(id+"F2.wireOp",EDGE,"E5"),sQuery(id+"F2.wireOp",EDGE,"E6"),sQuery(id+"F2.wireOp",EDGE,"E7")])]}),"instanceName":"8"}),"instanceName":"3"});
            var Q20;
            Q20=makeQuery(id+"F6.opPattern","COPY",BODY,{"derivedFrom":makeQuery(id+"F5.opPattern","COPY",BODY,{"derivedFrom":makeQuery(id+"F3.opExtrude","SWEPT_BODY",BODY,{"disambiguationData":[OSD([sQuery(id+"F2.wireOp",EDGE,"E2"),sQuery(id+"F2.wireOp",EDGE,"E3"),sQuery(id+"F2.wireOp",EDGE,"E4"),sQuery(id+"F2.wireOp",EDGE,"E5"),sQuery(id+"F2.wireOp",EDGE,"E6"),sQuery(id+"F2.wireOp",EDGE,"E7")])]}),"instanceName":"7"}),"instanceName":"3"});
            var Q21;
            Q21=makeQuery(id+"F6.opPattern","COPY",BODY,{"derivedFrom":makeQuery(id+"F5.opPattern","COPY",BODY,{"derivedFrom":makeQuery(id+"F3.opExtrude","SWEPT_BODY",BODY,{"disambiguationData":[OSD([sQuery(id+"F2.wireOp",EDGE,"E2"),sQuery(id+"F2.wireOp",EDGE,"E3"),sQuery(id+"F2.wireOp",EDGE,"E4"),sQuery(id+"F2.wireOp",EDGE,"E5"),sQuery(id+"F2.wireOp",EDGE,"E6"),sQuery(id+"F2.wireOp",EDGE,"E7")])]}),"instanceName":"6"}),"instanceName":"3"});
            var Q22;
            Q22=makeQuery(id+"F6.opPattern","COPY",BODY,{"derivedFrom":makeQuery(id+"F5.opPattern","COPY",BODY,{"derivedFrom":makeQuery(id+"F3.opExtrude","SWEPT_BODY",BODY,{"disambiguationData":[OSD([sQuery(id+"F2.wireOp",EDGE,"E2"),sQuery(id+"F2.wireOp",EDGE,"E3"),sQuery(id+"F2.wireOp",EDGE,"E4"),sQuery(id+"F2.wireOp",EDGE,"E5"),sQuery(id+"F2.wireOp",EDGE,"E6"),sQuery(id+"F2.wireOp",EDGE,"E7")])]}),"instanceName":"5"}),"instanceName":"3"});
            var Q23;
            Q23=makeQuery(id+"F6.opPattern","COPY",BODY,{"derivedFrom":makeQuery(id+"F4.opPattern","COPY",BODY,{"derivedFrom":makeQuery(id+"F3.opExtrude","SWEPT_BODY",BODY,{"disambiguationData":[OSD([sQuery(id+"F2.wireOp",EDGE,"E2"),sQuery(id+"F2.wireOp",EDGE,"E3"),sQuery(id+"F2.wireOp",EDGE,"E4"),sQuery(id+"F2.wireOp",EDGE,"E5"),sQuery(id+"F2.wireOp",EDGE,"E6"),sQuery(id+"F2.wireOp",EDGE,"E7")])]}),"instanceName":"4"}),"instanceName":"1"});
            var Q24;
            Q24=makeQuery(id+"F6.opPattern","COPY",BODY,{"derivedFrom":makeQuery(id+"F4.opPattern","COPY",BODY,{"derivedFrom":makeQuery(id+"F3.opExtrude","SWEPT_BODY",BODY,{"disambiguationData":[OSD([sQuery(id+"F2.wireOp",EDGE,"E2"),sQuery(id+"F2.wireOp",EDGE,"E3"),sQuery(id+"F2.wireOp",EDGE,"E4"),sQuery(id+"F2.wireOp",EDGE,"E5"),sQuery(id+"F2.wireOp",EDGE,"E6"),sQuery(id+"F2.wireOp",EDGE,"E7")])]}),"instanceName":"5"}),"instanceName":"1"});
            var Q25;
            Q25=makeQuery(id+"F6.opPattern","COPY",BODY,{"derivedFrom":makeQuery(id+"F4.opPattern","COPY",BODY,{"derivedFrom":makeQuery(id+"F3.opExtrude","SWEPT_BODY",BODY,{"disambiguationData":[OSD([sQuery(id+"F2.wireOp",EDGE,"E2"),sQuery(id+"F2.wireOp",EDGE,"E3"),sQuery(id+"F2.wireOp",EDGE,"E4"),sQuery(id+"F2.wireOp",EDGE,"E5"),sQuery(id+"F2.wireOp",EDGE,"E6"),sQuery(id+"F2.wireOp",EDGE,"E7")])]}),"instanceName":"6"}),"instanceName":"1"});
            var Q26;
            Q26=makeQuery(id+"F6.opPattern","COPY",BODY,{"derivedFrom":makeQuery(id+"F4.opPattern","COPY",BODY,{"derivedFrom":makeQuery(id+"F3.opExtrude","SWEPT_BODY",BODY,{"disambiguationData":[OSD([sQuery(id+"F2.wireOp",EDGE,"E2"),sQuery(id+"F2.wireOp",EDGE,"E3"),sQuery(id+"F2.wireOp",EDGE,"E4"),sQuery(id+"F2.wireOp",EDGE,"E5"),sQuery(id+"F2.wireOp",EDGE,"E6"),sQuery(id+"F2.wireOp",EDGE,"E7")])]}),"instanceName":"7"}),"instanceName":"1"});
            var Q27;
            Q27=makeQuery(id+"F6.opPattern","COPY",BODY,{"derivedFrom":makeQuery(id+"F4.opPattern","COPY",BODY,{"derivedFrom":makeQuery(id+"F3.opExtrude","SWEPT_BODY",BODY,{"disambiguationData":[OSD([sQuery(id+"F2.wireOp",EDGE,"E2"),sQuery(id+"F2.wireOp",EDGE,"E3"),sQuery(id+"F2.wireOp",EDGE,"E4"),sQuery(id+"F2.wireOp",EDGE,"E5"),sQuery(id+"F2.wireOp",EDGE,"E6"),sQuery(id+"F2.wireOp",EDGE,"E7")])]}),"instanceName":"8"}),"instanceName":"1"});
            var Q28;
            Q28=makeQuery(id+"F6.opPattern","COPY",BODY,{"derivedFrom":makeQuery(id+"F4.opPattern","COPY",BODY,{"derivedFrom":makeQuery(id+"F3.opExtrude","SWEPT_BODY",BODY,{"disambiguationData":[OSD([sQuery(id+"F2.wireOp",EDGE,"E2"),sQuery(id+"F2.wireOp",EDGE,"E3"),sQuery(id+"F2.wireOp",EDGE,"E4"),sQuery(id+"F2.wireOp",EDGE,"E5"),sQuery(id+"F2.wireOp",EDGE,"E6"),sQuery(id+"F2.wireOp",EDGE,"E7")])]}),"instanceName":"9"}),"instanceName":"1"});
            var Q29;
            Q29=makeQuery(id+"F6.opPattern","COPY",BODY,{"derivedFrom":makeQuery(id+"F4.opPattern","COPY",BODY,{"derivedFrom":makeQuery(id+"F3.opExtrude","SWEPT_BODY",BODY,{"disambiguationData":[OSD([sQuery(id+"F2.wireOp",EDGE,"E2"),sQuery(id+"F2.wireOp",EDGE,"E3"),sQuery(id+"F2.wireOp",EDGE,"E4"),sQuery(id+"F2.wireOp",EDGE,"E5"),sQuery(id+"F2.wireOp",EDGE,"E6"),sQuery(id+"F2.wireOp",EDGE,"E7")])]}),"instanceName":"10"}),"instanceName":"1"});
            var Q30;
            Q30=makeQuery(id+"F6.opPattern","COPY",BODY,{"derivedFrom":makeQuery(id+"F4.opPattern","COPY",BODY,{"derivedFrom":makeQuery(id+"F3.opExtrude","SWEPT_BODY",BODY,{"disambiguationData":[OSD([sQuery(id+"F2.wireOp",EDGE,"E2"),sQuery(id+"F2.wireOp",EDGE,"E3"),sQuery(id+"F2.wireOp",EDGE,"E4"),sQuery(id+"F2.wireOp",EDGE,"E5"),sQuery(id+"F2.wireOp",EDGE,"E6"),sQuery(id+"F2.wireOp",EDGE,"E7")])]}),"instanceName":"11"}),"instanceName":"1"});
            var Q31;
            Q31=makeQuery(id+"F6.opPattern","COPY",BODY,{"derivedFrom":makeQuery(id+"F4.opPattern","COPY",BODY,{"derivedFrom":makeQuery(id+"F3.opExtrude","SWEPT_BODY",BODY,{"disambiguationData":[OSD([sQuery(id+"F2.wireOp",EDGE,"E2"),sQuery(id+"F2.wireOp",EDGE,"E3"),sQuery(id+"F2.wireOp",EDGE,"E4"),sQuery(id+"F2.wireOp",EDGE,"E5"),sQuery(id+"F2.wireOp",EDGE,"E6"),sQuery(id+"F2.wireOp",EDGE,"E7")])]}),"instanceName":"12"}),"instanceName":"1"});
            var Q32;
            Q32=makeQuery(id+"F6.opPattern","COPY",BODY,{"derivedFrom":makeQuery(id+"F4.opPattern","COPY",BODY,{"derivedFrom":makeQuery(id+"F3.opExtrude","SWEPT_BODY",BODY,{"disambiguationData":[OSD([sQuery(id+"F2.wireOp",EDGE,"E2"),sQuery(id+"F2.wireOp",EDGE,"E3"),sQuery(id+"F2.wireOp",EDGE,"E4"),sQuery(id+"F2.wireOp",EDGE,"E5"),sQuery(id+"F2.wireOp",EDGE,"E6"),sQuery(id+"F2.wireOp",EDGE,"E7")])]}),"instanceName":"13"}),"instanceName":"1"});
            var Q33;
            Q33=makeQuery(id+"F6.opPattern","COPY",BODY,{"derivedFrom":makeQuery(id+"F4.opPattern","COPY",BODY,{"derivedFrom":makeQuery(id+"F3.opExtrude","SWEPT_BODY",BODY,{"disambiguationData":[OSD([sQuery(id+"F2.wireOp",EDGE,"E2"),sQuery(id+"F2.wireOp",EDGE,"E3"),sQuery(id+"F2.wireOp",EDGE,"E4"),sQuery(id+"F2.wireOp",EDGE,"E5"),sQuery(id+"F2.wireOp",EDGE,"E6"),sQuery(id+"F2.wireOp",EDGE,"E7")])]}),"instanceName":"14"}),"instanceName":"1"});
            var Q34;
            Q34=makeQuery(id+"F6.opPattern","COPY",BODY,{"derivedFrom":makeQuery(id+"F4.opPattern","COPY",BODY,{"derivedFrom":makeQuery(id+"F3.opExtrude","SWEPT_BODY",BODY,{"disambiguationData":[OSD([sQuery(id+"F2.wireOp",EDGE,"E2"),sQuery(id+"F2.wireOp",EDGE,"E3"),sQuery(id+"F2.wireOp",EDGE,"E4"),sQuery(id+"F2.wireOp",EDGE,"E5"),sQuery(id+"F2.wireOp",EDGE,"E6"),sQuery(id+"F2.wireOp",EDGE,"E7")])]}),"instanceName":"15"}),"instanceName":"1"});
            var Q35;
            Q35=makeQuery(id+"F6.opPattern","COPY",BODY,{"derivedFrom":makeQuery(id+"F4.opPattern","COPY",BODY,{"derivedFrom":makeQuery(id+"F3.opExtrude","SWEPT_BODY",BODY,{"disambiguationData":[OSD([sQuery(id+"F2.wireOp",EDGE,"E2"),sQuery(id+"F2.wireOp",EDGE,"E3"),sQuery(id+"F2.wireOp",EDGE,"E4"),sQuery(id+"F2.wireOp",EDGE,"E5"),sQuery(id+"F2.wireOp",EDGE,"E6"),sQuery(id+"F2.wireOp",EDGE,"E7")])]}),"instanceName":"16"}),"instanceName":"1"});
            var Q36;
            Q36=makeQuery(id+"F6.opPattern","COPY",BODY,{"derivedFrom":makeQuery(id+"F4.opPattern","COPY",BODY,{"derivedFrom":makeQuery(id+"F3.opExtrude","SWEPT_BODY",BODY,{"disambiguationData":[OSD([sQuery(id+"F2.wireOp",EDGE,"E2"),sQuery(id+"F2.wireOp",EDGE,"E3"),sQuery(id+"F2.wireOp",EDGE,"E4"),sQuery(id+"F2.wireOp",EDGE,"E5"),sQuery(id+"F2.wireOp",EDGE,"E6"),sQuery(id+"F2.wireOp",EDGE,"E7")])]}),"instanceName":"17"}),"instanceName":"1"});
            var Q37;
            Q37=makeQuery(id+"F6.opPattern","COPY",BODY,{"derivedFrom":makeQuery(id+"F4.opPattern","COPY",BODY,{"derivedFrom":makeQuery(id+"F3.opExtrude","SWEPT_BODY",BODY,{"disambiguationData":[OSD([sQuery(id+"F2.wireOp",EDGE,"E2"),sQuery(id+"F2.wireOp",EDGE,"E3"),sQuery(id+"F2.wireOp",EDGE,"E4"),sQuery(id+"F2.wireOp",EDGE,"E5"),sQuery(id+"F2.wireOp",EDGE,"E6"),sQuery(id+"F2.wireOp",EDGE,"E7")])]}),"instanceName":"18"}),"instanceName":"1"});
            var Q38;
            Q38=makeQuery(id+"F6.opPattern","COPY",BODY,{"derivedFrom":makeQuery(id+"F4.opPattern","COPY",BODY,{"derivedFrom":makeQuery(id+"F3.opExtrude","SWEPT_BODY",BODY,{"disambiguationData":[OSD([sQuery(id+"F2.wireOp",EDGE,"E2"),sQuery(id+"F2.wireOp",EDGE,"E3"),sQuery(id+"F2.wireOp",EDGE,"E4"),sQuery(id+"F2.wireOp",EDGE,"E5"),sQuery(id+"F2.wireOp",EDGE,"E6"),sQuery(id+"F2.wireOp",EDGE,"E7")])]}),"instanceName":"19"}),"instanceName":"1"});
            var Q39;
            Q39=makeQuery(id+"F6.opPattern","COPY",BODY,{"derivedFrom":makeQuery(id+"F4.opPattern","COPY",BODY,{"derivedFrom":makeQuery(id+"F3.opExtrude","SWEPT_BODY",BODY,{"disambiguationData":[OSD([sQuery(id+"F2.wireOp",EDGE,"E2"),sQuery(id+"F2.wireOp",EDGE,"E3"),sQuery(id+"F2.wireOp",EDGE,"E4"),sQuery(id+"F2.wireOp",EDGE,"E5"),sQuery(id+"F2.wireOp",EDGE,"E6"),sQuery(id+"F2.wireOp",EDGE,"E7")])]}),"instanceName":"20"}),"instanceName":"1"});
            var Q40;
            Q40=makeQuery(id+"F6.opPattern","COPY",BODY,{"derivedFrom":makeQuery(id+"F4.opPattern","COPY",BODY,{"derivedFrom":makeQuery(id+"F3.opExtrude","SWEPT_BODY",BODY,{"disambiguationData":[OSD([sQuery(id+"F2.wireOp",EDGE,"E2"),sQuery(id+"F2.wireOp",EDGE,"E3"),sQuery(id+"F2.wireOp",EDGE,"E4"),sQuery(id+"F2.wireOp",EDGE,"E5"),sQuery(id+"F2.wireOp",EDGE,"E6"),sQuery(id+"F2.wireOp",EDGE,"E7")])]}),"instanceName":"21"}),"instanceName":"1"});
            var Q41;
            Q41=makeQuery(id+"F6.opPattern","COPY",BODY,{"derivedFrom":makeQuery(id+"F4.opPattern","COPY",BODY,{"derivedFrom":makeQuery(id+"F3.opExtrude","SWEPT_BODY",BODY,{"disambiguationData":[OSD([sQuery(id+"F2.wireOp",EDGE,"E2"),sQuery(id+"F2.wireOp",EDGE,"E3"),sQuery(id+"F2.wireOp",EDGE,"E4"),sQuery(id+"F2.wireOp",EDGE,"E5"),sQuery(id+"F2.wireOp",EDGE,"E6"),sQuery(id+"F2.wireOp",EDGE,"E7")])]}),"instanceName":"22"}),"instanceName":"1"});
            var Q42;
            Q42=makeQuery(id+"F6.opPattern","COPY",BODY,{"derivedFrom":makeQuery(id+"F4.opPattern","COPY",BODY,{"derivedFrom":makeQuery(id+"F3.opExtrude","SWEPT_BODY",BODY,{"disambiguationData":[OSD([sQuery(id+"F2.wireOp",EDGE,"E2"),sQuery(id+"F2.wireOp",EDGE,"E3"),sQuery(id+"F2.wireOp",EDGE,"E4"),sQuery(id+"F2.wireOp",EDGE,"E5"),sQuery(id+"F2.wireOp",EDGE,"E6"),sQuery(id+"F2.wireOp",EDGE,"E7")])]}),"instanceName":"23"}),"instanceName":"1"});
            var Q43;
            Q43=makeQuery(id+"F6.opPattern","COPY",BODY,{"derivedFrom":makeQuery(id+"F4.opPattern","COPY",BODY,{"derivedFrom":makeQuery(id+"F3.opExtrude","SWEPT_BODY",BODY,{"disambiguationData":[OSD([sQuery(id+"F2.wireOp",EDGE,"E2"),sQuery(id+"F2.wireOp",EDGE,"E3"),sQuery(id+"F2.wireOp",EDGE,"E4"),sQuery(id+"F2.wireOp",EDGE,"E5"),sQuery(id+"F2.wireOp",EDGE,"E6"),sQuery(id+"F2.wireOp",EDGE,"E7")])]}),"instanceName":"24"}),"instanceName":"1"});
            var Q44;
            Q44=makeQuery(id+"F6.opPattern","COPY",BODY,{"derivedFrom":makeQuery(id+"F5.opPattern","COPY",BODY,{"derivedFrom":makeQuery(id+"F3.opExtrude","SWEPT_BODY",BODY,{"disambiguationData":[OSD([sQuery(id+"F2.wireOp",EDGE,"E2"),sQuery(id+"F2.wireOp",EDGE,"E3"),sQuery(id+"F2.wireOp",EDGE,"E4"),sQuery(id+"F2.wireOp",EDGE,"E5"),sQuery(id+"F2.wireOp",EDGE,"E6"),sQuery(id+"F2.wireOp",EDGE,"E7")])]}),"instanceName":"1"}),"instanceName":"1"});
            var Q45;
            Q45=makeQuery(id+"F6.opPattern","COPY",BODY,{"derivedFrom":makeQuery(id+"F5.opPattern","COPY",BODY,{"derivedFrom":makeQuery(id+"F3.opExtrude","SWEPT_BODY",BODY,{"disambiguationData":[OSD([sQuery(id+"F2.wireOp",EDGE,"E2"),sQuery(id+"F2.wireOp",EDGE,"E3"),sQuery(id+"F2.wireOp",EDGE,"E4"),sQuery(id+"F2.wireOp",EDGE,"E5"),sQuery(id+"F2.wireOp",EDGE,"E6"),sQuery(id+"F2.wireOp",EDGE,"E7")])]}),"instanceName":"2"}),"instanceName":"1"});
            var Q46;
            Q46=makeQuery(id+"F6.opPattern","COPY",BODY,{"derivedFrom":makeQuery(id+"F5.opPattern","COPY",BODY,{"derivedFrom":makeQuery(id+"F3.opExtrude","SWEPT_BODY",BODY,{"disambiguationData":[OSD([sQuery(id+"F2.wireOp",EDGE,"E2"),sQuery(id+"F2.wireOp",EDGE,"E3"),sQuery(id+"F2.wireOp",EDGE,"E4"),sQuery(id+"F2.wireOp",EDGE,"E5"),sQuery(id+"F2.wireOp",EDGE,"E6"),sQuery(id+"F2.wireOp",EDGE,"E7")])]}),"instanceName":"3"}),"instanceName":"1"});
            var Q47;
            Q47=makeQuery(id+"F6.opPattern","COPY",BODY,{"derivedFrom":makeQuery(id+"F5.opPattern","COPY",BODY,{"derivedFrom":makeQuery(id+"F3.opExtrude","SWEPT_BODY",BODY,{"disambiguationData":[OSD([sQuery(id+"F2.wireOp",EDGE,"E2"),sQuery(id+"F2.wireOp",EDGE,"E3"),sQuery(id+"F2.wireOp",EDGE,"E4"),sQuery(id+"F2.wireOp",EDGE,"E5"),sQuery(id+"F2.wireOp",EDGE,"E6"),sQuery(id+"F2.wireOp",EDGE,"E7")])]}),"instanceName":"4"}),"instanceName":"1"});
            var Q48;
            Q48=makeQuery(id+"F6.opPattern","COPY",BODY,{"derivedFrom":makeQuery(id+"F5.opPattern","COPY",BODY,{"derivedFrom":makeQuery(id+"F3.opExtrude","SWEPT_BODY",BODY,{"disambiguationData":[OSD([sQuery(id+"F2.wireOp",EDGE,"E2"),sQuery(id+"F2.wireOp",EDGE,"E3"),sQuery(id+"F2.wireOp",EDGE,"E4"),sQuery(id+"F2.wireOp",EDGE,"E5"),sQuery(id+"F2.wireOp",EDGE,"E6"),sQuery(id+"F2.wireOp",EDGE,"E7")])]}),"instanceName":"5"}),"instanceName":"1"});
            var Q49;
            Q49=makeQuery(id+"F6.opPattern","COPY",BODY,{"derivedFrom":makeQuery(id+"F5.opPattern","COPY",BODY,{"derivedFrom":makeQuery(id+"F3.opExtrude","SWEPT_BODY",BODY,{"disambiguationData":[OSD([sQuery(id+"F2.wireOp",EDGE,"E2"),sQuery(id+"F2.wireOp",EDGE,"E3"),sQuery(id+"F2.wireOp",EDGE,"E4"),sQuery(id+"F2.wireOp",EDGE,"E5"),sQuery(id+"F2.wireOp",EDGE,"E6"),sQuery(id+"F2.wireOp",EDGE,"E7")])]}),"instanceName":"6"}),"instanceName":"1"});
            var Q50;
            Q50=makeQuery(id+"F6.opPattern","COPY",BODY,{"derivedFrom":makeQuery(id+"F5.opPattern","COPY",BODY,{"derivedFrom":makeQuery(id+"F3.opExtrude","SWEPT_BODY",BODY,{"disambiguationData":[OSD([sQuery(id+"F2.wireOp",EDGE,"E2"),sQuery(id+"F2.wireOp",EDGE,"E3"),sQuery(id+"F2.wireOp",EDGE,"E4"),sQuery(id+"F2.wireOp",EDGE,"E5"),sQuery(id+"F2.wireOp",EDGE,"E6"),sQuery(id+"F2.wireOp",EDGE,"E7")])]}),"instanceName":"7"}),"instanceName":"1"});
            var Q51;
            Q51=makeQuery(id+"F6.opPattern","COPY",BODY,{"derivedFrom":makeQuery(id+"F5.opPattern","COPY",BODY,{"derivedFrom":makeQuery(id+"F3.opExtrude","SWEPT_BODY",BODY,{"disambiguationData":[OSD([sQuery(id+"F2.wireOp",EDGE,"E2"),sQuery(id+"F2.wireOp",EDGE,"E3"),sQuery(id+"F2.wireOp",EDGE,"E4"),sQuery(id+"F2.wireOp",EDGE,"E5"),sQuery(id+"F2.wireOp",EDGE,"E6"),sQuery(id+"F2.wireOp",EDGE,"E7")])]}),"instanceName":"8"}),"instanceName":"1"});
            var Q52;
            Q52=makeQuery(id+"F6.opPattern","COPY",BODY,{"derivedFrom":makeQuery(id+"F5.opPattern","COPY",BODY,{"derivedFrom":makeQuery(id+"F3.opExtrude","SWEPT_BODY",BODY,{"disambiguationData":[OSD([sQuery(id+"F2.wireOp",EDGE,"E2"),sQuery(id+"F2.wireOp",EDGE,"E3"),sQuery(id+"F2.wireOp",EDGE,"E4"),sQuery(id+"F2.wireOp",EDGE,"E5"),sQuery(id+"F2.wireOp",EDGE,"E6"),sQuery(id+"F2.wireOp",EDGE,"E7")])]}),"instanceName":"9"}),"instanceName":"1"});
            var Q53;
            Q53=makeQuery(id+"F6.opPattern","COPY",BODY,{"derivedFrom":makeQuery(id+"F5.opPattern","COPY",BODY,{"derivedFrom":makeQuery(id+"F3.opExtrude","SWEPT_BODY",BODY,{"disambiguationData":[OSD([sQuery(id+"F2.wireOp",EDGE,"E2"),sQuery(id+"F2.wireOp",EDGE,"E3"),sQuery(id+"F2.wireOp",EDGE,"E4"),sQuery(id+"F2.wireOp",EDGE,"E5"),sQuery(id+"F2.wireOp",EDGE,"E6"),sQuery(id+"F2.wireOp",EDGE,"E7")])]}),"instanceName":"10"}),"instanceName":"1"});
            var Q54;
            Q54=makeQuery(id+"F6.opPattern","COPY",BODY,{"derivedFrom":makeQuery(id+"F5.opPattern","COPY",BODY,{"derivedFrom":makeQuery(id+"F3.opExtrude","SWEPT_BODY",BODY,{"disambiguationData":[OSD([sQuery(id+"F2.wireOp",EDGE,"E2"),sQuery(id+"F2.wireOp",EDGE,"E3"),sQuery(id+"F2.wireOp",EDGE,"E4"),sQuery(id+"F2.wireOp",EDGE,"E5"),sQuery(id+"F2.wireOp",EDGE,"E6"),sQuery(id+"F2.wireOp",EDGE,"E7")])]}),"instanceName":"11"}),"instanceName":"1"});
            var Q55;
            Q55=makeQuery(id+"F6.opPattern","COPY",BODY,{"derivedFrom":makeQuery(id+"F5.opPattern","COPY",BODY,{"derivedFrom":makeQuery(id+"F3.opExtrude","SWEPT_BODY",BODY,{"disambiguationData":[OSD([sQuery(id+"F2.wireOp",EDGE,"E2"),sQuery(id+"F2.wireOp",EDGE,"E3"),sQuery(id+"F2.wireOp",EDGE,"E4"),sQuery(id+"F2.wireOp",EDGE,"E5"),sQuery(id+"F2.wireOp",EDGE,"E6"),sQuery(id+"F2.wireOp",EDGE,"E7")])]}),"instanceName":"12"}),"instanceName":"1"});
            var Q56;
            Q56=makeQuery(id+"F6.opPattern","COPY",BODY,{"derivedFrom":makeQuery(id+"F5.opPattern","COPY",BODY,{"derivedFrom":makeQuery(id+"F3.opExtrude","SWEPT_BODY",BODY,{"disambiguationData":[OSD([sQuery(id+"F2.wireOp",EDGE,"E2"),sQuery(id+"F2.wireOp",EDGE,"E3"),sQuery(id+"F2.wireOp",EDGE,"E4"),sQuery(id+"F2.wireOp",EDGE,"E5"),sQuery(id+"F2.wireOp",EDGE,"E6"),sQuery(id+"F2.wireOp",EDGE,"E7")])]}),"instanceName":"13"}),"instanceName":"1"});
            var Q57;
            Q57=makeQuery(id+"F6.opPattern","COPY",BODY,{"derivedFrom":makeQuery(id+"F5.opPattern","COPY",BODY,{"derivedFrom":makeQuery(id+"F3.opExtrude","SWEPT_BODY",BODY,{"disambiguationData":[OSD([sQuery(id+"F2.wireOp",EDGE,"E2"),sQuery(id+"F2.wireOp",EDGE,"E3"),sQuery(id+"F2.wireOp",EDGE,"E4"),sQuery(id+"F2.wireOp",EDGE,"E5"),sQuery(id+"F2.wireOp",EDGE,"E6"),sQuery(id+"F2.wireOp",EDGE,"E7")])]}),"instanceName":"14"}),"instanceName":"1"});
            var Q58;
            Q58=makeQuery(id+"F6.opPattern","COPY",BODY,{"derivedFrom":makeQuery(id+"F5.opPattern","COPY",BODY,{"derivedFrom":makeQuery(id+"F3.opExtrude","SWEPT_BODY",BODY,{"disambiguationData":[OSD([sQuery(id+"F2.wireOp",EDGE,"E2"),sQuery(id+"F2.wireOp",EDGE,"E3"),sQuery(id+"F2.wireOp",EDGE,"E4"),sQuery(id+"F2.wireOp",EDGE,"E5"),sQuery(id+"F2.wireOp",EDGE,"E6"),sQuery(id+"F2.wireOp",EDGE,"E7")])]}),"instanceName":"15"}),"instanceName":"1"});
            var Q59;
            Q59=makeQuery(id+"F6.opPattern","COPY",BODY,{"derivedFrom":makeQuery(id+"F5.opPattern","COPY",BODY,{"derivedFrom":makeQuery(id+"F3.opExtrude","SWEPT_BODY",BODY,{"disambiguationData":[OSD([sQuery(id+"F2.wireOp",EDGE,"E2"),sQuery(id+"F2.wireOp",EDGE,"E3"),sQuery(id+"F2.wireOp",EDGE,"E4"),sQuery(id+"F2.wireOp",EDGE,"E5"),sQuery(id+"F2.wireOp",EDGE,"E6"),sQuery(id+"F2.wireOp",EDGE,"E7")])]}),"instanceName":"16"}),"instanceName":"1"});
            var Q60;
            Q60=makeQuery(id+"F6.opPattern","COPY",BODY,{"derivedFrom":makeQuery(id+"F5.opPattern","COPY",BODY,{"derivedFrom":makeQuery(id+"F3.opExtrude","SWEPT_BODY",BODY,{"disambiguationData":[OSD([sQuery(id+"F2.wireOp",EDGE,"E2"),sQuery(id+"F2.wireOp",EDGE,"E3"),sQuery(id+"F2.wireOp",EDGE,"E4"),sQuery(id+"F2.wireOp",EDGE,"E5"),sQuery(id+"F2.wireOp",EDGE,"E6"),sQuery(id+"F2.wireOp",EDGE,"E7")])]}),"instanceName":"17"}),"instanceName":"1"});
            var Q61;
            Q61=makeQuery(id+"F6.opPattern","COPY",BODY,{"derivedFrom":makeQuery(id+"F5.opPattern","COPY",BODY,{"derivedFrom":makeQuery(id+"F3.opExtrude","SWEPT_BODY",BODY,{"disambiguationData":[OSD([sQuery(id+"F2.wireOp",EDGE,"E2"),sQuery(id+"F2.wireOp",EDGE,"E3"),sQuery(id+"F2.wireOp",EDGE,"E4"),sQuery(id+"F2.wireOp",EDGE,"E5"),sQuery(id+"F2.wireOp",EDGE,"E6"),sQuery(id+"F2.wireOp",EDGE,"E7")])]}),"instanceName":"18"}),"instanceName":"1"});
            var Q62;
            Q62=makeQuery(id+"F6.opPattern","COPY",BODY,{"derivedFrom":makeQuery(id+"F5.opPattern","COPY",BODY,{"derivedFrom":makeQuery(id+"F3.opExtrude","SWEPT_BODY",BODY,{"disambiguationData":[OSD([sQuery(id+"F2.wireOp",EDGE,"E2"),sQuery(id+"F2.wireOp",EDGE,"E3"),sQuery(id+"F2.wireOp",EDGE,"E4"),sQuery(id+"F2.wireOp",EDGE,"E5"),sQuery(id+"F2.wireOp",EDGE,"E6"),sQuery(id+"F2.wireOp",EDGE,"E7")])]}),"instanceName":"19"}),"instanceName":"1"});
            var Q63;
            Q63=makeQuery(id+"F6.opPattern","COPY",BODY,{"derivedFrom":makeQuery(id+"F5.opPattern","COPY",BODY,{"derivedFrom":makeQuery(id+"F3.opExtrude","SWEPT_BODY",BODY,{"disambiguationData":[OSD([sQuery(id+"F2.wireOp",EDGE,"E2"),sQuery(id+"F2.wireOp",EDGE,"E3"),sQuery(id+"F2.wireOp",EDGE,"E4"),sQuery(id+"F2.wireOp",EDGE,"E5"),sQuery(id+"F2.wireOp",EDGE,"E6"),sQuery(id+"F2.wireOp",EDGE,"E7")])]}),"instanceName":"20"}),"instanceName":"1"});
            var Q64;
            Q64=makeQuery(id+"F6.opPattern","COPY",BODY,{"derivedFrom":makeQuery(id+"F5.opPattern","COPY",BODY,{"derivedFrom":makeQuery(id+"F3.opExtrude","SWEPT_BODY",BODY,{"disambiguationData":[OSD([sQuery(id+"F2.wireOp",EDGE,"E2"),sQuery(id+"F2.wireOp",EDGE,"E3"),sQuery(id+"F2.wireOp",EDGE,"E4"),sQuery(id+"F2.wireOp",EDGE,"E5"),sQuery(id+"F2.wireOp",EDGE,"E6"),sQuery(id+"F2.wireOp",EDGE,"E7")])]}),"instanceName":"21"}),"instanceName":"1"});
            var Q65;
            Q65=makeQuery(id+"F6.opPattern","COPY",BODY,{"derivedFrom":makeQuery(id+"F5.opPattern","COPY",BODY,{"derivedFrom":makeQuery(id+"F3.opExtrude","SWEPT_BODY",BODY,{"disambiguationData":[OSD([sQuery(id+"F2.wireOp",EDGE,"E2"),sQuery(id+"F2.wireOp",EDGE,"E3"),sQuery(id+"F2.wireOp",EDGE,"E4"),sQuery(id+"F2.wireOp",EDGE,"E5"),sQuery(id+"F2.wireOp",EDGE,"E6"),sQuery(id+"F2.wireOp",EDGE,"E7")])]}),"instanceName":"22"}),"instanceName":"1"});
            var Q66;
            Q66=makeQuery(id+"F6.opPattern","COPY",BODY,{"derivedFrom":makeQuery(id+"F5.opPattern","COPY",BODY,{"derivedFrom":makeQuery(id+"F3.opExtrude","SWEPT_BODY",BODY,{"disambiguationData":[OSD([sQuery(id+"F2.wireOp",EDGE,"E2"),sQuery(id+"F2.wireOp",EDGE,"E3"),sQuery(id+"F2.wireOp",EDGE,"E4"),sQuery(id+"F2.wireOp",EDGE,"E5"),sQuery(id+"F2.wireOp",EDGE,"E6"),sQuery(id+"F2.wireOp",EDGE,"E7")])]}),"instanceName":"23"}),"instanceName":"1"});
            var Q67;
            Q67=makeQuery(id+"F6.opPattern","COPY",BODY,{"derivedFrom":makeQuery(id+"F5.opPattern","COPY",BODY,{"derivedFrom":makeQuery(id+"F3.opExtrude","SWEPT_BODY",BODY,{"disambiguationData":[OSD([sQuery(id+"F2.wireOp",EDGE,"E2"),sQuery(id+"F2.wireOp",EDGE,"E3"),sQuery(id+"F2.wireOp",EDGE,"E4"),sQuery(id+"F2.wireOp",EDGE,"E5"),sQuery(id+"F2.wireOp",EDGE,"E6"),sQuery(id+"F2.wireOp",EDGE,"E7")])]}),"instanceName":"24"}),"instanceName":"1"});
            var Q68;
            Q68=makeQuery(id+"F6.opPattern","COPY",BODY,{"derivedFrom":makeQuery(id+"F3.opExtrude","SWEPT_BODY",BODY,{"disambiguationData":[OSD([sQuery(id+"F2.wireOp",EDGE,"E2"),sQuery(id+"F2.wireOp",EDGE,"E3"),sQuery(id+"F2.wireOp",EDGE,"E4"),sQuery(id+"F2.wireOp",EDGE,"E5"),sQuery(id+"F2.wireOp",EDGE,"E6"),sQuery(id+"F2.wireOp",EDGE,"E7")])]}),"instanceName":"2"});
            var Q69;
            Q69=makeQuery(id+"F6.opPattern","COPY",BODY,{"derivedFrom":makeQuery(id+"F4.opPattern","COPY",BODY,{"derivedFrom":makeQuery(id+"F3.opExtrude","SWEPT_BODY",BODY,{"disambiguationData":[OSD([sQuery(id+"F2.wireOp",EDGE,"E2"),sQuery(id+"F2.wireOp",EDGE,"E3"),sQuery(id+"F2.wireOp",EDGE,"E4"),sQuery(id+"F2.wireOp",EDGE,"E5"),sQuery(id+"F2.wireOp",EDGE,"E6"),sQuery(id+"F2.wireOp",EDGE,"E7")])]}),"instanceName":"1"}),"instanceName":"2"});
            var Q70;
            Q70=makeQuery(id+"F6.opPattern","COPY",BODY,{"derivedFrom":makeQuery(id+"F4.opPattern","COPY",BODY,{"derivedFrom":makeQuery(id+"F3.opExtrude","SWEPT_BODY",BODY,{"disambiguationData":[OSD([sQuery(id+"F2.wireOp",EDGE,"E2"),sQuery(id+"F2.wireOp",EDGE,"E3"),sQuery(id+"F2.wireOp",EDGE,"E4"),sQuery(id+"F2.wireOp",EDGE,"E5"),sQuery(id+"F2.wireOp",EDGE,"E6"),sQuery(id+"F2.wireOp",EDGE,"E7")])]}),"instanceName":"2"}),"instanceName":"2"});
            var Q71;
            Q71=makeQuery(id+"F6.opPattern","COPY",BODY,{"derivedFrom":makeQuery(id+"F4.opPattern","COPY",BODY,{"derivedFrom":makeQuery(id+"F3.opExtrude","SWEPT_BODY",BODY,{"disambiguationData":[OSD([sQuery(id+"F2.wireOp",EDGE,"E2"),sQuery(id+"F2.wireOp",EDGE,"E3"),sQuery(id+"F2.wireOp",EDGE,"E4"),sQuery(id+"F2.wireOp",EDGE,"E5"),sQuery(id+"F2.wireOp",EDGE,"E6"),sQuery(id+"F2.wireOp",EDGE,"E7")])]}),"instanceName":"3"}),"instanceName":"2"});
            var Q72;
            Q72=makeQuery(id+"F6.opPattern","COPY",BODY,{"derivedFrom":makeQuery(id+"F4.opPattern","COPY",BODY,{"derivedFrom":makeQuery(id+"F3.opExtrude","SWEPT_BODY",BODY,{"disambiguationData":[OSD([sQuery(id+"F2.wireOp",EDGE,"E2"),sQuery(id+"F2.wireOp",EDGE,"E3"),sQuery(id+"F2.wireOp",EDGE,"E4"),sQuery(id+"F2.wireOp",EDGE,"E5"),sQuery(id+"F2.wireOp",EDGE,"E6"),sQuery(id+"F2.wireOp",EDGE,"E7")])]}),"instanceName":"4"}),"instanceName":"2"});
            var Q73;
            Q73=makeQuery(id+"F6.opPattern","COPY",BODY,{"derivedFrom":makeQuery(id+"F4.opPattern","COPY",BODY,{"derivedFrom":makeQuery(id+"F3.opExtrude","SWEPT_BODY",BODY,{"disambiguationData":[OSD([sQuery(id+"F2.wireOp",EDGE,"E2"),sQuery(id+"F2.wireOp",EDGE,"E3"),sQuery(id+"F2.wireOp",EDGE,"E4"),sQuery(id+"F2.wireOp",EDGE,"E5"),sQuery(id+"F2.wireOp",EDGE,"E6"),sQuery(id+"F2.wireOp",EDGE,"E7")])]}),"instanceName":"5"}),"instanceName":"2"});
            var Q74;
            Q74=makeQuery(id+"F6.opPattern","COPY",BODY,{"derivedFrom":makeQuery(id+"F4.opPattern","COPY",BODY,{"derivedFrom":makeQuery(id+"F3.opExtrude","SWEPT_BODY",BODY,{"disambiguationData":[OSD([sQuery(id+"F2.wireOp",EDGE,"E2"),sQuery(id+"F2.wireOp",EDGE,"E3"),sQuery(id+"F2.wireOp",EDGE,"E4"),sQuery(id+"F2.wireOp",EDGE,"E5"),sQuery(id+"F2.wireOp",EDGE,"E6"),sQuery(id+"F2.wireOp",EDGE,"E7")])]}),"instanceName":"6"}),"instanceName":"2"});
            var Q75;
            Q75=makeQuery(id+"F6.opPattern","COPY",BODY,{"derivedFrom":makeQuery(id+"F4.opPattern","COPY",BODY,{"derivedFrom":makeQuery(id+"F3.opExtrude","SWEPT_BODY",BODY,{"disambiguationData":[OSD([sQuery(id+"F2.wireOp",EDGE,"E2"),sQuery(id+"F2.wireOp",EDGE,"E3"),sQuery(id+"F2.wireOp",EDGE,"E4"),sQuery(id+"F2.wireOp",EDGE,"E5"),sQuery(id+"F2.wireOp",EDGE,"E6"),sQuery(id+"F2.wireOp",EDGE,"E7")])]}),"instanceName":"7"}),"instanceName":"2"});
            var Q76;
            Q76=makeQuery(id+"F6.opPattern","COPY",BODY,{"derivedFrom":makeQuery(id+"F4.opPattern","COPY",BODY,{"derivedFrom":makeQuery(id+"F3.opExtrude","SWEPT_BODY",BODY,{"disambiguationData":[OSD([sQuery(id+"F2.wireOp",EDGE,"E2"),sQuery(id+"F2.wireOp",EDGE,"E3"),sQuery(id+"F2.wireOp",EDGE,"E4"),sQuery(id+"F2.wireOp",EDGE,"E5"),sQuery(id+"F2.wireOp",EDGE,"E6"),sQuery(id+"F2.wireOp",EDGE,"E7")])]}),"instanceName":"8"}),"instanceName":"2"});
            var Q77;
            Q77=makeQuery(id+"F6.opPattern","COPY",BODY,{"derivedFrom":makeQuery(id+"F4.opPattern","COPY",BODY,{"derivedFrom":makeQuery(id+"F3.opExtrude","SWEPT_BODY",BODY,{"disambiguationData":[OSD([sQuery(id+"F2.wireOp",EDGE,"E2"),sQuery(id+"F2.wireOp",EDGE,"E3"),sQuery(id+"F2.wireOp",EDGE,"E4"),sQuery(id+"F2.wireOp",EDGE,"E5"),sQuery(id+"F2.wireOp",EDGE,"E6"),sQuery(id+"F2.wireOp",EDGE,"E7")])]}),"instanceName":"9"}),"instanceName":"2"});
            var Q78;
            Q78=makeQuery(id+"F6.opPattern","COPY",BODY,{"derivedFrom":makeQuery(id+"F4.opPattern","COPY",BODY,{"derivedFrom":makeQuery(id+"F3.opExtrude","SWEPT_BODY",BODY,{"disambiguationData":[OSD([sQuery(id+"F2.wireOp",EDGE,"E2"),sQuery(id+"F2.wireOp",EDGE,"E3"),sQuery(id+"F2.wireOp",EDGE,"E4"),sQuery(id+"F2.wireOp",EDGE,"E5"),sQuery(id+"F2.wireOp",EDGE,"E6"),sQuery(id+"F2.wireOp",EDGE,"E7")])]}),"instanceName":"10"}),"instanceName":"2"});
            var Q79;
            Q79=makeQuery(id+"F6.opPattern","COPY",BODY,{"derivedFrom":makeQuery(id+"F4.opPattern","COPY",BODY,{"derivedFrom":makeQuery(id+"F3.opExtrude","SWEPT_BODY",BODY,{"disambiguationData":[OSD([sQuery(id+"F2.wireOp",EDGE,"E2"),sQuery(id+"F2.wireOp",EDGE,"E3"),sQuery(id+"F2.wireOp",EDGE,"E4"),sQuery(id+"F2.wireOp",EDGE,"E5"),sQuery(id+"F2.wireOp",EDGE,"E6"),sQuery(id+"F2.wireOp",EDGE,"E7")])]}),"instanceName":"11"}),"instanceName":"2"});
            var Q80;
            Q80=makeQuery(id+"F6.opPattern","COPY",BODY,{"derivedFrom":makeQuery(id+"F4.opPattern","COPY",BODY,{"derivedFrom":makeQuery(id+"F3.opExtrude","SWEPT_BODY",BODY,{"disambiguationData":[OSD([sQuery(id+"F2.wireOp",EDGE,"E2"),sQuery(id+"F2.wireOp",EDGE,"E3"),sQuery(id+"F2.wireOp",EDGE,"E4"),sQuery(id+"F2.wireOp",EDGE,"E5"),sQuery(id+"F2.wireOp",EDGE,"E6"),sQuery(id+"F2.wireOp",EDGE,"E7")])]}),"instanceName":"12"}),"instanceName":"2"});
            var Q81;
            Q81=makeQuery(id+"F6.opPattern","COPY",BODY,{"derivedFrom":makeQuery(id+"F4.opPattern","COPY",BODY,{"derivedFrom":makeQuery(id+"F3.opExtrude","SWEPT_BODY",BODY,{"disambiguationData":[OSD([sQuery(id+"F2.wireOp",EDGE,"E2"),sQuery(id+"F2.wireOp",EDGE,"E3"),sQuery(id+"F2.wireOp",EDGE,"E4"),sQuery(id+"F2.wireOp",EDGE,"E5"),sQuery(id+"F2.wireOp",EDGE,"E6"),sQuery(id+"F2.wireOp",EDGE,"E7")])]}),"instanceName":"13"}),"instanceName":"2"});
            var Q82;
            Q82=makeQuery(id+"F6.opPattern","COPY",BODY,{"derivedFrom":makeQuery(id+"F4.opPattern","COPY",BODY,{"derivedFrom":makeQuery(id+"F3.opExtrude","SWEPT_BODY",BODY,{"disambiguationData":[OSD([sQuery(id+"F2.wireOp",EDGE,"E2"),sQuery(id+"F2.wireOp",EDGE,"E3"),sQuery(id+"F2.wireOp",EDGE,"E4"),sQuery(id+"F2.wireOp",EDGE,"E5"),sQuery(id+"F2.wireOp",EDGE,"E6"),sQuery(id+"F2.wireOp",EDGE,"E7")])]}),"instanceName":"14"}),"instanceName":"2"});
            var Q83;
            Q83=makeQuery(id+"F6.opPattern","COPY",BODY,{"derivedFrom":makeQuery(id+"F4.opPattern","COPY",BODY,{"derivedFrom":makeQuery(id+"F3.opExtrude","SWEPT_BODY",BODY,{"disambiguationData":[OSD([sQuery(id+"F2.wireOp",EDGE,"E2"),sQuery(id+"F2.wireOp",EDGE,"E3"),sQuery(id+"F2.wireOp",EDGE,"E4"),sQuery(id+"F2.wireOp",EDGE,"E5"),sQuery(id+"F2.wireOp",EDGE,"E6"),sQuery(id+"F2.wireOp",EDGE,"E7")])]}),"instanceName":"15"}),"instanceName":"2"});
            var Q84;
            Q84=makeQuery(id+"F6.opPattern","COPY",BODY,{"derivedFrom":makeQuery(id+"F4.opPattern","COPY",BODY,{"derivedFrom":makeQuery(id+"F3.opExtrude","SWEPT_BODY",BODY,{"disambiguationData":[OSD([sQuery(id+"F2.wireOp",EDGE,"E2"),sQuery(id+"F2.wireOp",EDGE,"E3"),sQuery(id+"F2.wireOp",EDGE,"E4"),sQuery(id+"F2.wireOp",EDGE,"E5"),sQuery(id+"F2.wireOp",EDGE,"E6"),sQuery(id+"F2.wireOp",EDGE,"E7")])]}),"instanceName":"16"}),"instanceName":"2"});
            var Q85;
            Q85=makeQuery(id+"F6.opPattern","COPY",BODY,{"derivedFrom":makeQuery(id+"F4.opPattern","COPY",BODY,{"derivedFrom":makeQuery(id+"F3.opExtrude","SWEPT_BODY",BODY,{"disambiguationData":[OSD([sQuery(id+"F2.wireOp",EDGE,"E2"),sQuery(id+"F2.wireOp",EDGE,"E3"),sQuery(id+"F2.wireOp",EDGE,"E4"),sQuery(id+"F2.wireOp",EDGE,"E5"),sQuery(id+"F2.wireOp",EDGE,"E6"),sQuery(id+"F2.wireOp",EDGE,"E7")])]}),"instanceName":"17"}),"instanceName":"2"});
            var Q86;
            Q86=makeQuery(id+"F6.opPattern","COPY",BODY,{"derivedFrom":makeQuery(id+"F4.opPattern","COPY",BODY,{"derivedFrom":makeQuery(id+"F3.opExtrude","SWEPT_BODY",BODY,{"disambiguationData":[OSD([sQuery(id+"F2.wireOp",EDGE,"E2"),sQuery(id+"F2.wireOp",EDGE,"E3"),sQuery(id+"F2.wireOp",EDGE,"E4"),sQuery(id+"F2.wireOp",EDGE,"E5"),sQuery(id+"F2.wireOp",EDGE,"E6"),sQuery(id+"F2.wireOp",EDGE,"E7")])]}),"instanceName":"18"}),"instanceName":"2"});
            var Q87;
            Q87=makeQuery(id+"F6.opPattern","COPY",BODY,{"derivedFrom":makeQuery(id+"F4.opPattern","COPY",BODY,{"derivedFrom":makeQuery(id+"F3.opExtrude","SWEPT_BODY",BODY,{"disambiguationData":[OSD([sQuery(id+"F2.wireOp",EDGE,"E2"),sQuery(id+"F2.wireOp",EDGE,"E3"),sQuery(id+"F2.wireOp",EDGE,"E4"),sQuery(id+"F2.wireOp",EDGE,"E5"),sQuery(id+"F2.wireOp",EDGE,"E6"),sQuery(id+"F2.wireOp",EDGE,"E7")])]}),"instanceName":"19"}),"instanceName":"2"});
            var Q88;
            Q88=makeQuery(id+"F6.opPattern","COPY",BODY,{"derivedFrom":makeQuery(id+"F4.opPattern","COPY",BODY,{"derivedFrom":makeQuery(id+"F3.opExtrude","SWEPT_BODY",BODY,{"disambiguationData":[OSD([sQuery(id+"F2.wireOp",EDGE,"E2"),sQuery(id+"F2.wireOp",EDGE,"E3"),sQuery(id+"F2.wireOp",EDGE,"E4"),sQuery(id+"F2.wireOp",EDGE,"E5"),sQuery(id+"F2.wireOp",EDGE,"E6"),sQuery(id+"F2.wireOp",EDGE,"E7")])]}),"instanceName":"20"}),"instanceName":"2"});
            var Q89;
            Q89=makeQuery(id+"F6.opPattern","COPY",BODY,{"derivedFrom":makeQuery(id+"F4.opPattern","COPY",BODY,{"derivedFrom":makeQuery(id+"F3.opExtrude","SWEPT_BODY",BODY,{"disambiguationData":[OSD([sQuery(id+"F2.wireOp",EDGE,"E2"),sQuery(id+"F2.wireOp",EDGE,"E3"),sQuery(id+"F2.wireOp",EDGE,"E4"),sQuery(id+"F2.wireOp",EDGE,"E5"),sQuery(id+"F2.wireOp",EDGE,"E6"),sQuery(id+"F2.wireOp",EDGE,"E7")])]}),"instanceName":"21"}),"instanceName":"2"});
            var Q90;
            Q90=makeQuery(id+"F6.opPattern","COPY",BODY,{"derivedFrom":makeQuery(id+"F4.opPattern","COPY",BODY,{"derivedFrom":makeQuery(id+"F3.opExtrude","SWEPT_BODY",BODY,{"disambiguationData":[OSD([sQuery(id+"F2.wireOp",EDGE,"E2"),sQuery(id+"F2.wireOp",EDGE,"E3"),sQuery(id+"F2.wireOp",EDGE,"E4"),sQuery(id+"F2.wireOp",EDGE,"E5"),sQuery(id+"F2.wireOp",EDGE,"E6"),sQuery(id+"F2.wireOp",EDGE,"E7")])]}),"instanceName":"22"}),"instanceName":"2"});
            var Q91;
            Q91=makeQuery(id+"F6.opPattern","COPY",BODY,{"derivedFrom":makeQuery(id+"F4.opPattern","COPY",BODY,{"derivedFrom":makeQuery(id+"F3.opExtrude","SWEPT_BODY",BODY,{"disambiguationData":[OSD([sQuery(id+"F2.wireOp",EDGE,"E2"),sQuery(id+"F2.wireOp",EDGE,"E3"),sQuery(id+"F2.wireOp",EDGE,"E4"),sQuery(id+"F2.wireOp",EDGE,"E5"),sQuery(id+"F2.wireOp",EDGE,"E6"),sQuery(id+"F2.wireOp",EDGE,"E7")])]}),"instanceName":"23"}),"instanceName":"2"});
            var Q92;
            Q92=makeQuery(id+"F6.opPattern","COPY",BODY,{"derivedFrom":makeQuery(id+"F4.opPattern","COPY",BODY,{"derivedFrom":makeQuery(id+"F3.opExtrude","SWEPT_BODY",BODY,{"disambiguationData":[OSD([sQuery(id+"F2.wireOp",EDGE,"E2"),sQuery(id+"F2.wireOp",EDGE,"E3"),sQuery(id+"F2.wireOp",EDGE,"E4"),sQuery(id+"F2.wireOp",EDGE,"E5"),sQuery(id+"F2.wireOp",EDGE,"E6"),sQuery(id+"F2.wireOp",EDGE,"E7")])]}),"instanceName":"24"}),"instanceName":"2"});
            var Q93;
            Q93=makeQuery(id+"F6.opPattern","COPY",BODY,{"derivedFrom":makeQuery(id+"F5.opPattern","COPY",BODY,{"derivedFrom":makeQuery(id+"F3.opExtrude","SWEPT_BODY",BODY,{"disambiguationData":[OSD([sQuery(id+"F2.wireOp",EDGE,"E2"),sQuery(id+"F2.wireOp",EDGE,"E3"),sQuery(id+"F2.wireOp",EDGE,"E4"),sQuery(id+"F2.wireOp",EDGE,"E5"),sQuery(id+"F2.wireOp",EDGE,"E6"),sQuery(id+"F2.wireOp",EDGE,"E7")])]}),"instanceName":"1"}),"instanceName":"2"});
            var Q94;
            Q94=makeQuery(id+"F6.opPattern","COPY",BODY,{"derivedFrom":makeQuery(id+"F5.opPattern","COPY",BODY,{"derivedFrom":makeQuery(id+"F3.opExtrude","SWEPT_BODY",BODY,{"disambiguationData":[OSD([sQuery(id+"F2.wireOp",EDGE,"E2"),sQuery(id+"F2.wireOp",EDGE,"E3"),sQuery(id+"F2.wireOp",EDGE,"E4"),sQuery(id+"F2.wireOp",EDGE,"E5"),sQuery(id+"F2.wireOp",EDGE,"E6"),sQuery(id+"F2.wireOp",EDGE,"E7")])]}),"instanceName":"2"}),"instanceName":"2"});
            var Q95;
            Q95=makeQuery(id+"F6.opPattern","COPY",BODY,{"derivedFrom":makeQuery(id+"F5.opPattern","COPY",BODY,{"derivedFrom":makeQuery(id+"F3.opExtrude","SWEPT_BODY",BODY,{"disambiguationData":[OSD([sQuery(id+"F2.wireOp",EDGE,"E2"),sQuery(id+"F2.wireOp",EDGE,"E3"),sQuery(id+"F2.wireOp",EDGE,"E4"),sQuery(id+"F2.wireOp",EDGE,"E5"),sQuery(id+"F2.wireOp",EDGE,"E6"),sQuery(id+"F2.wireOp",EDGE,"E7")])]}),"instanceName":"3"}),"instanceName":"2"});
            var Q96;
            Q96=makeQuery(id+"F6.opPattern","COPY",BODY,{"derivedFrom":makeQuery(id+"F5.opPattern","COPY",BODY,{"derivedFrom":makeQuery(id+"F3.opExtrude","SWEPT_BODY",BODY,{"disambiguationData":[OSD([sQuery(id+"F2.wireOp",EDGE,"E2"),sQuery(id+"F2.wireOp",EDGE,"E3"),sQuery(id+"F2.wireOp",EDGE,"E4"),sQuery(id+"F2.wireOp",EDGE,"E5"),sQuery(id+"F2.wireOp",EDGE,"E6"),sQuery(id+"F2.wireOp",EDGE,"E7")])]}),"instanceName":"4"}),"instanceName":"2"});
            var Q97;
            Q97=makeQuery(id+"F6.opPattern","COPY",BODY,{"derivedFrom":makeQuery(id+"F5.opPattern","COPY",BODY,{"derivedFrom":makeQuery(id+"F3.opExtrude","SWEPT_BODY",BODY,{"disambiguationData":[OSD([sQuery(id+"F2.wireOp",EDGE,"E2"),sQuery(id+"F2.wireOp",EDGE,"E3"),sQuery(id+"F2.wireOp",EDGE,"E4"),sQuery(id+"F2.wireOp",EDGE,"E5"),sQuery(id+"F2.wireOp",EDGE,"E6"),sQuery(id+"F2.wireOp",EDGE,"E7")])]}),"instanceName":"5"}),"instanceName":"2"});
            var Q98;
            Q98=makeQuery(id+"F6.opPattern","COPY",BODY,{"derivedFrom":makeQuery(id+"F5.opPattern","COPY",BODY,{"derivedFrom":makeQuery(id+"F3.opExtrude","SWEPT_BODY",BODY,{"disambiguationData":[OSD([sQuery(id+"F2.wireOp",EDGE,"E2"),sQuery(id+"F2.wireOp",EDGE,"E3"),sQuery(id+"F2.wireOp",EDGE,"E4"),sQuery(id+"F2.wireOp",EDGE,"E5"),sQuery(id+"F2.wireOp",EDGE,"E6"),sQuery(id+"F2.wireOp",EDGE,"E7")])]}),"instanceName":"6"}),"instanceName":"2"});
            var Q99;
            Q99=makeQuery(id+"F6.opPattern","COPY",BODY,{"derivedFrom":makeQuery(id+"F5.opPattern","COPY",BODY,{"derivedFrom":makeQuery(id+"F3.opExtrude","SWEPT_BODY",BODY,{"disambiguationData":[OSD([sQuery(id+"F2.wireOp",EDGE,"E2"),sQuery(id+"F2.wireOp",EDGE,"E3"),sQuery(id+"F2.wireOp",EDGE,"E4"),sQuery(id+"F2.wireOp",EDGE,"E5"),sQuery(id+"F2.wireOp",EDGE,"E6"),sQuery(id+"F2.wireOp",EDGE,"E7")])]}),"instanceName":"7"}),"instanceName":"2"});
            var Q100;
            Q100=makeQuery(id+"F6.opPattern","COPY",BODY,{"derivedFrom":makeQuery(id+"F5.opPattern","COPY",BODY,{"derivedFrom":makeQuery(id+"F3.opExtrude","SWEPT_BODY",BODY,{"disambiguationData":[OSD([sQuery(id+"F2.wireOp",EDGE,"E2"),sQuery(id+"F2.wireOp",EDGE,"E3"),sQuery(id+"F2.wireOp",EDGE,"E4"),sQuery(id+"F2.wireOp",EDGE,"E5"),sQuery(id+"F2.wireOp",EDGE,"E6"),sQuery(id+"F2.wireOp",EDGE,"E7")])]}),"instanceName":"8"}),"instanceName":"2"});
            var Q101;
            Q101=makeQuery(id+"F6.opPattern","COPY",BODY,{"derivedFrom":makeQuery(id+"F5.opPattern","COPY",BODY,{"derivedFrom":makeQuery(id+"F3.opExtrude","SWEPT_BODY",BODY,{"disambiguationData":[OSD([sQuery(id+"F2.wireOp",EDGE,"E2"),sQuery(id+"F2.wireOp",EDGE,"E3"),sQuery(id+"F2.wireOp",EDGE,"E4"),sQuery(id+"F2.wireOp",EDGE,"E5"),sQuery(id+"F2.wireOp",EDGE,"E6"),sQuery(id+"F2.wireOp",EDGE,"E7")])]}),"instanceName":"9"}),"instanceName":"2"});
            var Q102;
            Q102=makeQuery(id+"F6.opPattern","COPY",BODY,{"derivedFrom":makeQuery(id+"F5.opPattern","COPY",BODY,{"derivedFrom":makeQuery(id+"F3.opExtrude","SWEPT_BODY",BODY,{"disambiguationData":[OSD([sQuery(id+"F2.wireOp",EDGE,"E2"),sQuery(id+"F2.wireOp",EDGE,"E3"),sQuery(id+"F2.wireOp",EDGE,"E4"),sQuery(id+"F2.wireOp",EDGE,"E5"),sQuery(id+"F2.wireOp",EDGE,"E6"),sQuery(id+"F2.wireOp",EDGE,"E7")])]}),"instanceName":"10"}),"instanceName":"2"});
            var Q103;
            Q103=makeQuery(id+"F6.opPattern","COPY",BODY,{"derivedFrom":makeQuery(id+"F5.opPattern","COPY",BODY,{"derivedFrom":makeQuery(id+"F3.opExtrude","SWEPT_BODY",BODY,{"disambiguationData":[OSD([sQuery(id+"F2.wireOp",EDGE,"E2"),sQuery(id+"F2.wireOp",EDGE,"E3"),sQuery(id+"F2.wireOp",EDGE,"E4"),sQuery(id+"F2.wireOp",EDGE,"E5"),sQuery(id+"F2.wireOp",EDGE,"E6"),sQuery(id+"F2.wireOp",EDGE,"E7")])]}),"instanceName":"11"}),"instanceName":"2"});
            var Q104;
            Q104=makeQuery(id+"F6.opPattern","COPY",BODY,{"derivedFrom":makeQuery(id+"F5.opPattern","COPY",BODY,{"derivedFrom":makeQuery(id+"F3.opExtrude","SWEPT_BODY",BODY,{"disambiguationData":[OSD([sQuery(id+"F2.wireOp",EDGE,"E2"),sQuery(id+"F2.wireOp",EDGE,"E3"),sQuery(id+"F2.wireOp",EDGE,"E4"),sQuery(id+"F2.wireOp",EDGE,"E5"),sQuery(id+"F2.wireOp",EDGE,"E6"),sQuery(id+"F2.wireOp",EDGE,"E7")])]}),"instanceName":"12"}),"instanceName":"2"});
            var Q105;
            Q105=makeQuery(id+"F6.opPattern","COPY",BODY,{"derivedFrom":makeQuery(id+"F5.opPattern","COPY",BODY,{"derivedFrom":makeQuery(id+"F3.opExtrude","SWEPT_BODY",BODY,{"disambiguationData":[OSD([sQuery(id+"F2.wireOp",EDGE,"E2"),sQuery(id+"F2.wireOp",EDGE,"E3"),sQuery(id+"F2.wireOp",EDGE,"E4"),sQuery(id+"F2.wireOp",EDGE,"E5"),sQuery(id+"F2.wireOp",EDGE,"E6"),sQuery(id+"F2.wireOp",EDGE,"E7")])]}),"instanceName":"13"}),"instanceName":"2"});
            var Q106;
            Q106=makeQuery(id+"F6.opPattern","COPY",BODY,{"derivedFrom":makeQuery(id+"F5.opPattern","COPY",BODY,{"derivedFrom":makeQuery(id+"F3.opExtrude","SWEPT_BODY",BODY,{"disambiguationData":[OSD([sQuery(id+"F2.wireOp",EDGE,"E2"),sQuery(id+"F2.wireOp",EDGE,"E3"),sQuery(id+"F2.wireOp",EDGE,"E4"),sQuery(id+"F2.wireOp",EDGE,"E5"),sQuery(id+"F2.wireOp",EDGE,"E6"),sQuery(id+"F2.wireOp",EDGE,"E7")])]}),"instanceName":"14"}),"instanceName":"2"});
            var Q107;
            Q107=makeQuery(id+"F6.opPattern","COPY",BODY,{"derivedFrom":makeQuery(id+"F5.opPattern","COPY",BODY,{"derivedFrom":makeQuery(id+"F3.opExtrude","SWEPT_BODY",BODY,{"disambiguationData":[OSD([sQuery(id+"F2.wireOp",EDGE,"E2"),sQuery(id+"F2.wireOp",EDGE,"E3"),sQuery(id+"F2.wireOp",EDGE,"E4"),sQuery(id+"F2.wireOp",EDGE,"E5"),sQuery(id+"F2.wireOp",EDGE,"E6"),sQuery(id+"F2.wireOp",EDGE,"E7")])]}),"instanceName":"15"}),"instanceName":"2"});
            var Q108;
            Q108=makeQuery(id+"F6.opPattern","COPY",BODY,{"derivedFrom":makeQuery(id+"F5.opPattern","COPY",BODY,{"derivedFrom":makeQuery(id+"F3.opExtrude","SWEPT_BODY",BODY,{"disambiguationData":[OSD([sQuery(id+"F2.wireOp",EDGE,"E2"),sQuery(id+"F2.wireOp",EDGE,"E3"),sQuery(id+"F2.wireOp",EDGE,"E4"),sQuery(id+"F2.wireOp",EDGE,"E5"),sQuery(id+"F2.wireOp",EDGE,"E6"),sQuery(id+"F2.wireOp",EDGE,"E7")])]}),"instanceName":"16"}),"instanceName":"2"});
            var Q109;
            Q109=makeQuery(id+"F6.opPattern","COPY",BODY,{"derivedFrom":makeQuery(id+"F5.opPattern","COPY",BODY,{"derivedFrom":makeQuery(id+"F3.opExtrude","SWEPT_BODY",BODY,{"disambiguationData":[OSD([sQuery(id+"F2.wireOp",EDGE,"E2"),sQuery(id+"F2.wireOp",EDGE,"E3"),sQuery(id+"F2.wireOp",EDGE,"E4"),sQuery(id+"F2.wireOp",EDGE,"E5"),sQuery(id+"F2.wireOp",EDGE,"E6"),sQuery(id+"F2.wireOp",EDGE,"E7")])]}),"instanceName":"17"}),"instanceName":"2"});
            var Q110;
            Q110=makeQuery(id+"F6.opPattern","COPY",BODY,{"derivedFrom":makeQuery(id+"F5.opPattern","COPY",BODY,{"derivedFrom":makeQuery(id+"F3.opExtrude","SWEPT_BODY",BODY,{"disambiguationData":[OSD([sQuery(id+"F2.wireOp",EDGE,"E2"),sQuery(id+"F2.wireOp",EDGE,"E3"),sQuery(id+"F2.wireOp",EDGE,"E4"),sQuery(id+"F2.wireOp",EDGE,"E5"),sQuery(id+"F2.wireOp",EDGE,"E6"),sQuery(id+"F2.wireOp",EDGE,"E7")])]}),"instanceName":"18"}),"instanceName":"2"});
            var Q111;
            Q111=makeQuery(id+"F6.opPattern","COPY",BODY,{"derivedFrom":makeQuery(id+"F5.opPattern","COPY",BODY,{"derivedFrom":makeQuery(id+"F3.opExtrude","SWEPT_BODY",BODY,{"disambiguationData":[OSD([sQuery(id+"F2.wireOp",EDGE,"E2"),sQuery(id+"F2.wireOp",EDGE,"E3"),sQuery(id+"F2.wireOp",EDGE,"E4"),sQuery(id+"F2.wireOp",EDGE,"E5"),sQuery(id+"F2.wireOp",EDGE,"E6"),sQuery(id+"F2.wireOp",EDGE,"E7")])]}),"instanceName":"19"}),"instanceName":"2"});
            var Q112;
            Q112=makeQuery(id+"F6.opPattern","COPY",BODY,{"derivedFrom":makeQuery(id+"F5.opPattern","COPY",BODY,{"derivedFrom":makeQuery(id+"F3.opExtrude","SWEPT_BODY",BODY,{"disambiguationData":[OSD([sQuery(id+"F2.wireOp",EDGE,"E2"),sQuery(id+"F2.wireOp",EDGE,"E3"),sQuery(id+"F2.wireOp",EDGE,"E4"),sQuery(id+"F2.wireOp",EDGE,"E5"),sQuery(id+"F2.wireOp",EDGE,"E6"),sQuery(id+"F2.wireOp",EDGE,"E7")])]}),"instanceName":"20"}),"instanceName":"2"});
            var Q113;
            Q113=makeQuery(id+"F6.opPattern","COPY",BODY,{"derivedFrom":makeQuery(id+"F5.opPattern","COPY",BODY,{"derivedFrom":makeQuery(id+"F3.opExtrude","SWEPT_BODY",BODY,{"disambiguationData":[OSD([sQuery(id+"F2.wireOp",EDGE,"E2"),sQuery(id+"F2.wireOp",EDGE,"E3"),sQuery(id+"F2.wireOp",EDGE,"E4"),sQuery(id+"F2.wireOp",EDGE,"E5"),sQuery(id+"F2.wireOp",EDGE,"E6"),sQuery(id+"F2.wireOp",EDGE,"E7")])]}),"instanceName":"21"}),"instanceName":"2"});
            var Q114;
            Q114=makeQuery(id+"F6.opPattern","COPY",BODY,{"derivedFrom":makeQuery(id+"F5.opPattern","COPY",BODY,{"derivedFrom":makeQuery(id+"F3.opExtrude","SWEPT_BODY",BODY,{"disambiguationData":[OSD([sQuery(id+"F2.wireOp",EDGE,"E2"),sQuery(id+"F2.wireOp",EDGE,"E3"),sQuery(id+"F2.wireOp",EDGE,"E4"),sQuery(id+"F2.wireOp",EDGE,"E5"),sQuery(id+"F2.wireOp",EDGE,"E6"),sQuery(id+"F2.wireOp",EDGE,"E7")])]}),"instanceName":"22"}),"instanceName":"2"});
            var Q115;
            Q115=makeQuery(id+"F6.opPattern","COPY",BODY,{"derivedFrom":makeQuery(id+"F5.opPattern","COPY",BODY,{"derivedFrom":makeQuery(id+"F3.opExtrude","SWEPT_BODY",BODY,{"disambiguationData":[OSD([sQuery(id+"F2.wireOp",EDGE,"E2"),sQuery(id+"F2.wireOp",EDGE,"E3"),sQuery(id+"F2.wireOp",EDGE,"E4"),sQuery(id+"F2.wireOp",EDGE,"E5"),sQuery(id+"F2.wireOp",EDGE,"E6"),sQuery(id+"F2.wireOp",EDGE,"E7")])]}),"instanceName":"23"}),"instanceName":"2"});
            var Q116;
            Q116=makeQuery(id+"F6.opPattern","COPY",BODY,{"derivedFrom":makeQuery(id+"F5.opPattern","COPY",BODY,{"derivedFrom":makeQuery(id+"F3.opExtrude","SWEPT_BODY",BODY,{"disambiguationData":[OSD([sQuery(id+"F2.wireOp",EDGE,"E2"),sQuery(id+"F2.wireOp",EDGE,"E3"),sQuery(id+"F2.wireOp",EDGE,"E4"),sQuery(id+"F2.wireOp",EDGE,"E5"),sQuery(id+"F2.wireOp",EDGE,"E6"),sQuery(id+"F2.wireOp",EDGE,"E7")])]}),"instanceName":"24"}),"instanceName":"2"});
            var Q117;
            Q117=makeQuery(id+"F6.opPattern","COPY",BODY,{"derivedFrom":makeQuery(id+"F3.opExtrude","SWEPT_BODY",BODY,{"disambiguationData":[OSD([sQuery(id+"F2.wireOp",EDGE,"E2"),sQuery(id+"F2.wireOp",EDGE,"E3"),sQuery(id+"F2.wireOp",EDGE,"E4"),sQuery(id+"F2.wireOp",EDGE,"E5"),sQuery(id+"F2.wireOp",EDGE,"E6"),sQuery(id+"F2.wireOp",EDGE,"E7")])]}),"instanceName":"3"});
            var Q118;
            Q118=makeQuery(id+"F6.opPattern","COPY",BODY,{"derivedFrom":makeQuery(id+"F4.opPattern","COPY",BODY,{"derivedFrom":makeQuery(id+"F3.opExtrude","SWEPT_BODY",BODY,{"disambiguationData":[OSD([sQuery(id+"F2.wireOp",EDGE,"E2"),sQuery(id+"F2.wireOp",EDGE,"E3"),sQuery(id+"F2.wireOp",EDGE,"E4"),sQuery(id+"F2.wireOp",EDGE,"E5"),sQuery(id+"F2.wireOp",EDGE,"E6"),sQuery(id+"F2.wireOp",EDGE,"E7")])]}),"instanceName":"1"}),"instanceName":"3"});
            var Q119;
            Q119=makeQuery(id+"F6.opPattern","COPY",BODY,{"derivedFrom":makeQuery(id+"F4.opPattern","COPY",BODY,{"derivedFrom":makeQuery(id+"F3.opExtrude","SWEPT_BODY",BODY,{"disambiguationData":[OSD([sQuery(id+"F2.wireOp",EDGE,"E2"),sQuery(id+"F2.wireOp",EDGE,"E3"),sQuery(id+"F2.wireOp",EDGE,"E4"),sQuery(id+"F2.wireOp",EDGE,"E5"),sQuery(id+"F2.wireOp",EDGE,"E6"),sQuery(id+"F2.wireOp",EDGE,"E7")])]}),"instanceName":"2"}),"instanceName":"3"});
            var Q120;
            Q120=makeQuery(id+"F6.opPattern","COPY",BODY,{"derivedFrom":makeQuery(id+"F4.opPattern","COPY",BODY,{"derivedFrom":makeQuery(id+"F3.opExtrude","SWEPT_BODY",BODY,{"disambiguationData":[OSD([sQuery(id+"F2.wireOp",EDGE,"E2"),sQuery(id+"F2.wireOp",EDGE,"E3"),sQuery(id+"F2.wireOp",EDGE,"E4"),sQuery(id+"F2.wireOp",EDGE,"E5"),sQuery(id+"F2.wireOp",EDGE,"E6"),sQuery(id+"F2.wireOp",EDGE,"E7")])]}),"instanceName":"3"}),"instanceName":"3"});
            var Q121;
            Q121=makeQuery(id+"F6.opPattern","COPY",BODY,{"derivedFrom":makeQuery(id+"F4.opPattern","COPY",BODY,{"derivedFrom":makeQuery(id+"F3.opExtrude","SWEPT_BODY",BODY,{"disambiguationData":[OSD([sQuery(id+"F2.wireOp",EDGE,"E2"),sQuery(id+"F2.wireOp",EDGE,"E3"),sQuery(id+"F2.wireOp",EDGE,"E4"),sQuery(id+"F2.wireOp",EDGE,"E5"),sQuery(id+"F2.wireOp",EDGE,"E6"),sQuery(id+"F2.wireOp",EDGE,"E7")])]}),"instanceName":"4"}),"instanceName":"3"});
            var Q122;
            Q122=makeQuery(id+"F6.opPattern","COPY",BODY,{"derivedFrom":makeQuery(id+"F4.opPattern","COPY",BODY,{"derivedFrom":makeQuery(id+"F3.opExtrude","SWEPT_BODY",BODY,{"disambiguationData":[OSD([sQuery(id+"F2.wireOp",EDGE,"E2"),sQuery(id+"F2.wireOp",EDGE,"E3"),sQuery(id+"F2.wireOp",EDGE,"E4"),sQuery(id+"F2.wireOp",EDGE,"E5"),sQuery(id+"F2.wireOp",EDGE,"E6"),sQuery(id+"F2.wireOp",EDGE,"E7")])]}),"instanceName":"5"}),"instanceName":"3"});
            var Q123;
            Q123=makeQuery(id+"F6.opPattern","COPY",BODY,{"derivedFrom":makeQuery(id+"F4.opPattern","COPY",BODY,{"derivedFrom":makeQuery(id+"F3.opExtrude","SWEPT_BODY",BODY,{"disambiguationData":[OSD([sQuery(id+"F2.wireOp",EDGE,"E2"),sQuery(id+"F2.wireOp",EDGE,"E3"),sQuery(id+"F2.wireOp",EDGE,"E4"),sQuery(id+"F2.wireOp",EDGE,"E5"),sQuery(id+"F2.wireOp",EDGE,"E6"),sQuery(id+"F2.wireOp",EDGE,"E7")])]}),"instanceName":"6"}),"instanceName":"3"});
            var Q124;
            Q124=makeQuery(id+"F6.opPattern","COPY",BODY,{"derivedFrom":makeQuery(id+"F4.opPattern","COPY",BODY,{"derivedFrom":makeQuery(id+"F3.opExtrude","SWEPT_BODY",BODY,{"disambiguationData":[OSD([sQuery(id+"F2.wireOp",EDGE,"E2"),sQuery(id+"F2.wireOp",EDGE,"E3"),sQuery(id+"F2.wireOp",EDGE,"E4"),sQuery(id+"F2.wireOp",EDGE,"E5"),sQuery(id+"F2.wireOp",EDGE,"E6"),sQuery(id+"F2.wireOp",EDGE,"E7")])]}),"instanceName":"7"}),"instanceName":"3"});
            var Q125;
            Q125=makeQuery(id+"F6.opPattern","COPY",BODY,{"derivedFrom":makeQuery(id+"F4.opPattern","COPY",BODY,{"derivedFrom":makeQuery(id+"F3.opExtrude","SWEPT_BODY",BODY,{"disambiguationData":[OSD([sQuery(id+"F2.wireOp",EDGE,"E2"),sQuery(id+"F2.wireOp",EDGE,"E3"),sQuery(id+"F2.wireOp",EDGE,"E4"),sQuery(id+"F2.wireOp",EDGE,"E5"),sQuery(id+"F2.wireOp",EDGE,"E6"),sQuery(id+"F2.wireOp",EDGE,"E7")])]}),"instanceName":"8"}),"instanceName":"3"});
            var Q126;
            Q126=makeQuery(id+"F6.opPattern","COPY",BODY,{"derivedFrom":makeQuery(id+"F4.opPattern","COPY",BODY,{"derivedFrom":makeQuery(id+"F3.opExtrude","SWEPT_BODY",BODY,{"disambiguationData":[OSD([sQuery(id+"F2.wireOp",EDGE,"E2"),sQuery(id+"F2.wireOp",EDGE,"E3"),sQuery(id+"F2.wireOp",EDGE,"E4"),sQuery(id+"F2.wireOp",EDGE,"E5"),sQuery(id+"F2.wireOp",EDGE,"E6"),sQuery(id+"F2.wireOp",EDGE,"E7")])]}),"instanceName":"9"}),"instanceName":"3"});
            var Q127;
            Q127=makeQuery(id+"F6.opPattern","COPY",BODY,{"derivedFrom":makeQuery(id+"F4.opPattern","COPY",BODY,{"derivedFrom":makeQuery(id+"F3.opExtrude","SWEPT_BODY",BODY,{"disambiguationData":[OSD([sQuery(id+"F2.wireOp",EDGE,"E2"),sQuery(id+"F2.wireOp",EDGE,"E3"),sQuery(id+"F2.wireOp",EDGE,"E4"),sQuery(id+"F2.wireOp",EDGE,"E5"),sQuery(id+"F2.wireOp",EDGE,"E6"),sQuery(id+"F2.wireOp",EDGE,"E7")])]}),"instanceName":"10"}),"instanceName":"3"});
            var Q128;
            Q128=makeQuery(id+"F6.opPattern","COPY",BODY,{"derivedFrom":makeQuery(id+"F4.opPattern","COPY",BODY,{"derivedFrom":makeQuery(id+"F3.opExtrude","SWEPT_BODY",BODY,{"disambiguationData":[OSD([sQuery(id+"F2.wireOp",EDGE,"E2"),sQuery(id+"F2.wireOp",EDGE,"E3"),sQuery(id+"F2.wireOp",EDGE,"E4"),sQuery(id+"F2.wireOp",EDGE,"E5"),sQuery(id+"F2.wireOp",EDGE,"E6"),sQuery(id+"F2.wireOp",EDGE,"E7")])]}),"instanceName":"11"}),"instanceName":"3"});
            var Q129;
            Q129=makeQuery(id+"F6.opPattern","COPY",BODY,{"derivedFrom":makeQuery(id+"F4.opPattern","COPY",BODY,{"derivedFrom":makeQuery(id+"F3.opExtrude","SWEPT_BODY",BODY,{"disambiguationData":[OSD([sQuery(id+"F2.wireOp",EDGE,"E2"),sQuery(id+"F2.wireOp",EDGE,"E3"),sQuery(id+"F2.wireOp",EDGE,"E4"),sQuery(id+"F2.wireOp",EDGE,"E5"),sQuery(id+"F2.wireOp",EDGE,"E6"),sQuery(id+"F2.wireOp",EDGE,"E7")])]}),"instanceName":"12"}),"instanceName":"3"});
            var Q130;
            Q130=makeQuery(id+"F6.opPattern","COPY",BODY,{"derivedFrom":makeQuery(id+"F4.opPattern","COPY",BODY,{"derivedFrom":makeQuery(id+"F3.opExtrude","SWEPT_BODY",BODY,{"disambiguationData":[OSD([sQuery(id+"F2.wireOp",EDGE,"E2"),sQuery(id+"F2.wireOp",EDGE,"E3"),sQuery(id+"F2.wireOp",EDGE,"E4"),sQuery(id+"F2.wireOp",EDGE,"E5"),sQuery(id+"F2.wireOp",EDGE,"E6"),sQuery(id+"F2.wireOp",EDGE,"E7")])]}),"instanceName":"13"}),"instanceName":"3"});
            var Q131;
            Q131=makeQuery(id+"F6.opPattern","COPY",BODY,{"derivedFrom":makeQuery(id+"F4.opPattern","COPY",BODY,{"derivedFrom":makeQuery(id+"F3.opExtrude","SWEPT_BODY",BODY,{"disambiguationData":[OSD([sQuery(id+"F2.wireOp",EDGE,"E2"),sQuery(id+"F2.wireOp",EDGE,"E3"),sQuery(id+"F2.wireOp",EDGE,"E4"),sQuery(id+"F2.wireOp",EDGE,"E5"),sQuery(id+"F2.wireOp",EDGE,"E6"),sQuery(id+"F2.wireOp",EDGE,"E7")])]}),"instanceName":"14"}),"instanceName":"3"});
            var Q132;
            Q132=makeQuery(id+"F6.opPattern","COPY",BODY,{"derivedFrom":makeQuery(id+"F4.opPattern","COPY",BODY,{"derivedFrom":makeQuery(id+"F3.opExtrude","SWEPT_BODY",BODY,{"disambiguationData":[OSD([sQuery(id+"F2.wireOp",EDGE,"E2"),sQuery(id+"F2.wireOp",EDGE,"E3"),sQuery(id+"F2.wireOp",EDGE,"E4"),sQuery(id+"F2.wireOp",EDGE,"E5"),sQuery(id+"F2.wireOp",EDGE,"E6"),sQuery(id+"F2.wireOp",EDGE,"E7")])]}),"instanceName":"15"}),"instanceName":"3"});
            var Q133;
            Q133=makeQuery(id+"F6.opPattern","COPY",BODY,{"derivedFrom":makeQuery(id+"F4.opPattern","COPY",BODY,{"derivedFrom":makeQuery(id+"F3.opExtrude","SWEPT_BODY",BODY,{"disambiguationData":[OSD([sQuery(id+"F2.wireOp",EDGE,"E2"),sQuery(id+"F2.wireOp",EDGE,"E3"),sQuery(id+"F2.wireOp",EDGE,"E4"),sQuery(id+"F2.wireOp",EDGE,"E5"),sQuery(id+"F2.wireOp",EDGE,"E6"),sQuery(id+"F2.wireOp",EDGE,"E7")])]}),"instanceName":"16"}),"instanceName":"3"});
            var Q134;
            Q134=makeQuery(id+"F6.opPattern","COPY",BODY,{"derivedFrom":makeQuery(id+"F4.opPattern","COPY",BODY,{"derivedFrom":makeQuery(id+"F3.opExtrude","SWEPT_BODY",BODY,{"disambiguationData":[OSD([sQuery(id+"F2.wireOp",EDGE,"E2"),sQuery(id+"F2.wireOp",EDGE,"E3"),sQuery(id+"F2.wireOp",EDGE,"E4"),sQuery(id+"F2.wireOp",EDGE,"E5"),sQuery(id+"F2.wireOp",EDGE,"E6"),sQuery(id+"F2.wireOp",EDGE,"E7")])]}),"instanceName":"17"}),"instanceName":"3"});
            var Q135;
            Q135=makeQuery(id+"F6.opPattern","COPY",BODY,{"derivedFrom":makeQuery(id+"F4.opPattern","COPY",BODY,{"derivedFrom":makeQuery(id+"F3.opExtrude","SWEPT_BODY",BODY,{"disambiguationData":[OSD([sQuery(id+"F2.wireOp",EDGE,"E2"),sQuery(id+"F2.wireOp",EDGE,"E3"),sQuery(id+"F2.wireOp",EDGE,"E4"),sQuery(id+"F2.wireOp",EDGE,"E5"),sQuery(id+"F2.wireOp",EDGE,"E6"),sQuery(id+"F2.wireOp",EDGE,"E7")])]}),"instanceName":"18"}),"instanceName":"3"});
            var Q136;
            Q136=makeQuery(id+"F6.opPattern","COPY",BODY,{"derivedFrom":makeQuery(id+"F4.opPattern","COPY",BODY,{"derivedFrom":makeQuery(id+"F3.opExtrude","SWEPT_BODY",BODY,{"disambiguationData":[OSD([sQuery(id+"F2.wireOp",EDGE,"E2"),sQuery(id+"F2.wireOp",EDGE,"E3"),sQuery(id+"F2.wireOp",EDGE,"E4"),sQuery(id+"F2.wireOp",EDGE,"E5"),sQuery(id+"F2.wireOp",EDGE,"E6"),sQuery(id+"F2.wireOp",EDGE,"E7")])]}),"instanceName":"19"}),"instanceName":"3"});
            var Q137;
            Q137=makeQuery(id+"F6.opPattern","COPY",BODY,{"derivedFrom":makeQuery(id+"F4.opPattern","COPY",BODY,{"derivedFrom":makeQuery(id+"F3.opExtrude","SWEPT_BODY",BODY,{"disambiguationData":[OSD([sQuery(id+"F2.wireOp",EDGE,"E2"),sQuery(id+"F2.wireOp",EDGE,"E3"),sQuery(id+"F2.wireOp",EDGE,"E4"),sQuery(id+"F2.wireOp",EDGE,"E5"),sQuery(id+"F2.wireOp",EDGE,"E6"),sQuery(id+"F2.wireOp",EDGE,"E7")])]}),"instanceName":"20"}),"instanceName":"3"});
            var Q138;
            Q138=makeQuery(id+"F6.opPattern","COPY",BODY,{"derivedFrom":makeQuery(id+"F4.opPattern","COPY",BODY,{"derivedFrom":makeQuery(id+"F3.opExtrude","SWEPT_BODY",BODY,{"disambiguationData":[OSD([sQuery(id+"F2.wireOp",EDGE,"E2"),sQuery(id+"F2.wireOp",EDGE,"E3"),sQuery(id+"F2.wireOp",EDGE,"E4"),sQuery(id+"F2.wireOp",EDGE,"E5"),sQuery(id+"F2.wireOp",EDGE,"E6"),sQuery(id+"F2.wireOp",EDGE,"E7")])]}),"instanceName":"21"}),"instanceName":"3"});
            var Q139;
            Q139=makeQuery(id+"F6.opPattern","COPY",BODY,{"derivedFrom":makeQuery(id+"F4.opPattern","COPY",BODY,{"derivedFrom":makeQuery(id+"F3.opExtrude","SWEPT_BODY",BODY,{"disambiguationData":[OSD([sQuery(id+"F2.wireOp",EDGE,"E2"),sQuery(id+"F2.wireOp",EDGE,"E3"),sQuery(id+"F2.wireOp",EDGE,"E4"),sQuery(id+"F2.wireOp",EDGE,"E5"),sQuery(id+"F2.wireOp",EDGE,"E6"),sQuery(id+"F2.wireOp",EDGE,"E7")])]}),"instanceName":"22"}),"instanceName":"3"});
            var Q140;
            Q140=makeQuery(id+"F6.opPattern","COPY",BODY,{"derivedFrom":makeQuery(id+"F4.opPattern","COPY",BODY,{"derivedFrom":makeQuery(id+"F3.opExtrude","SWEPT_BODY",BODY,{"disambiguationData":[OSD([sQuery(id+"F2.wireOp",EDGE,"E2"),sQuery(id+"F2.wireOp",EDGE,"E3"),sQuery(id+"F2.wireOp",EDGE,"E4"),sQuery(id+"F2.wireOp",EDGE,"E5"),sQuery(id+"F2.wireOp",EDGE,"E6"),sQuery(id+"F2.wireOp",EDGE,"E7")])]}),"instanceName":"23"}),"instanceName":"3"});
            var Q141;
            Q141=makeQuery(id+"F6.opPattern","COPY",BODY,{"derivedFrom":makeQuery(id+"F4.opPattern","COPY",BODY,{"derivedFrom":makeQuery(id+"F3.opExtrude","SWEPT_BODY",BODY,{"disambiguationData":[OSD([sQuery(id+"F2.wireOp",EDGE,"E2"),sQuery(id+"F2.wireOp",EDGE,"E3"),sQuery(id+"F2.wireOp",EDGE,"E4"),sQuery(id+"F2.wireOp",EDGE,"E5"),sQuery(id+"F2.wireOp",EDGE,"E6"),sQuery(id+"F2.wireOp",EDGE,"E7")])]}),"instanceName":"2"}),"instanceName":"1"});
            var Q142;
            Q142=makeQuery(id+"F4.opPattern","COPY",BODY,{"derivedFrom":makeQuery(id+"F3.opExtrude","SWEPT_BODY",BODY,{"disambiguationData":[OSD([sQuery(id+"F2.wireOp",EDGE,"E2"),sQuery(id+"F2.wireOp",EDGE,"E3"),sQuery(id+"F2.wireOp",EDGE,"E4"),sQuery(id+"F2.wireOp",EDGE,"E5"),sQuery(id+"F2.wireOp",EDGE,"E6"),sQuery(id+"F2.wireOp",EDGE,"E7")])]}),"instanceName":"5"});
            var Q143;
            Q143=makeQuery(id+"F4.opPattern","COPY",BODY,{"derivedFrom":makeQuery(id+"F3.opExtrude","SWEPT_BODY",BODY,{"disambiguationData":[OSD([sQuery(id+"F2.wireOp",EDGE,"E2"),sQuery(id+"F2.wireOp",EDGE,"E3"),sQuery(id+"F2.wireOp",EDGE,"E4"),sQuery(id+"F2.wireOp",EDGE,"E5"),sQuery(id+"F2.wireOp",EDGE,"E6"),sQuery(id+"F2.wireOp",EDGE,"E7")])]}),"instanceName":"6"});
            var Q144;
            Q144=makeQuery(id+"F5.opPattern","COPY",BODY,{"derivedFrom":makeQuery(id+"F3.opExtrude","SWEPT_BODY",BODY,{"disambiguationData":[OSD([sQuery(id+"F2.wireOp",EDGE,"E2"),sQuery(id+"F2.wireOp",EDGE,"E3"),sQuery(id+"F2.wireOp",EDGE,"E4"),sQuery(id+"F2.wireOp",EDGE,"E5"),sQuery(id+"F2.wireOp",EDGE,"E6"),sQuery(id+"F2.wireOp",EDGE,"E7")])]}),"instanceName":"21"});
            var Q145;
            Q145=makeQuery(id+"F5.opPattern","COPY",BODY,{"derivedFrom":makeQuery(id+"F3.opExtrude","SWEPT_BODY",BODY,{"disambiguationData":[OSD([sQuery(id+"F2.wireOp",EDGE,"E2"),sQuery(id+"F2.wireOp",EDGE,"E3"),sQuery(id+"F2.wireOp",EDGE,"E4"),sQuery(id+"F2.wireOp",EDGE,"E5"),sQuery(id+"F2.wireOp",EDGE,"E6"),sQuery(id+"F2.wireOp",EDGE,"E7")])]}),"instanceName":"1"});
            var Q146;
            Q146=makeQuery(id+"F5.opPattern","COPY",BODY,{"derivedFrom":makeQuery(id+"F3.opExtrude","SWEPT_BODY",BODY,{"disambiguationData":[OSD([sQuery(id+"F2.wireOp",EDGE,"E2"),sQuery(id+"F2.wireOp",EDGE,"E3"),sQuery(id+"F2.wireOp",EDGE,"E4"),sQuery(id+"F2.wireOp",EDGE,"E5"),sQuery(id+"F2.wireOp",EDGE,"E6"),sQuery(id+"F2.wireOp",EDGE,"E7")])]}),"instanceName":"15"});
            var Q147;
            Q147=makeQuery(id+"F5.opPattern","COPY",BODY,{"derivedFrom":makeQuery(id+"F3.opExtrude","SWEPT_BODY",BODY,{"disambiguationData":[OSD([sQuery(id+"F2.wireOp",EDGE,"E2"),sQuery(id+"F2.wireOp",EDGE,"E3"),sQuery(id+"F2.wireOp",EDGE,"E4"),sQuery(id+"F2.wireOp",EDGE,"E5"),sQuery(id+"F2.wireOp",EDGE,"E6"),sQuery(id+"F2.wireOp",EDGE,"E7")])]}),"instanceName":"14"});
            var Q148;
            Q148=makeQuery(id+"F5.opPattern","COPY",BODY,{"derivedFrom":makeQuery(id+"F3.opExtrude","SWEPT_BODY",BODY,{"disambiguationData":[OSD([sQuery(id+"F2.wireOp",EDGE,"E2"),sQuery(id+"F2.wireOp",EDGE,"E3"),sQuery(id+"F2.wireOp",EDGE,"E4"),sQuery(id+"F2.wireOp",EDGE,"E5"),sQuery(id+"F2.wireOp",EDGE,"E6"),sQuery(id+"F2.wireOp",EDGE,"E7")])]}),"instanceName":"13"});
            var Q149;
            Q149=makeQuery(id+"F5.opPattern","COPY",BODY,{"derivedFrom":makeQuery(id+"F3.opExtrude","SWEPT_BODY",BODY,{"disambiguationData":[OSD([sQuery(id+"F2.wireOp",EDGE,"E2"),sQuery(id+"F2.wireOp",EDGE,"E3"),sQuery(id+"F2.wireOp",EDGE,"E4"),sQuery(id+"F2.wireOp",EDGE,"E5"),sQuery(id+"F2.wireOp",EDGE,"E6"),sQuery(id+"F2.wireOp",EDGE,"E7")])]}),"instanceName":"12"});
            var Q150;
            Q150=makeQuery(id+"F5.opPattern","COPY",BODY,{"derivedFrom":makeQuery(id+"F3.opExtrude","SWEPT_BODY",BODY,{"disambiguationData":[OSD([sQuery(id+"F2.wireOp",EDGE,"E2"),sQuery(id+"F2.wireOp",EDGE,"E3"),sQuery(id+"F2.wireOp",EDGE,"E4"),sQuery(id+"F2.wireOp",EDGE,"E5"),sQuery(id+"F2.wireOp",EDGE,"E6"),sQuery(id+"F2.wireOp",EDGE,"E7")])]}),"instanceName":"11"});
            var Q151;
            Q151=makeQuery(id+"F5.opPattern","COPY",BODY,{"derivedFrom":makeQuery(id+"F3.opExtrude","SWEPT_BODY",BODY,{"disambiguationData":[OSD([sQuery(id+"F2.wireOp",EDGE,"E2"),sQuery(id+"F2.wireOp",EDGE,"E3"),sQuery(id+"F2.wireOp",EDGE,"E4"),sQuery(id+"F2.wireOp",EDGE,"E5"),sQuery(id+"F2.wireOp",EDGE,"E6"),sQuery(id+"F2.wireOp",EDGE,"E7")])]}),"instanceName":"10"});
            var Q152;
            Q152=makeQuery(id+"F5.opPattern","COPY",BODY,{"derivedFrom":makeQuery(id+"F3.opExtrude","SWEPT_BODY",BODY,{"disambiguationData":[OSD([sQuery(id+"F2.wireOp",EDGE,"E2"),sQuery(id+"F2.wireOp",EDGE,"E3"),sQuery(id+"F2.wireOp",EDGE,"E4"),sQuery(id+"F2.wireOp",EDGE,"E5"),sQuery(id+"F2.wireOp",EDGE,"E6"),sQuery(id+"F2.wireOp",EDGE,"E7")])]}),"instanceName":"17"});
            var Q153;
            Q153=makeQuery(id+"F5.opPattern","COPY",BODY,{"derivedFrom":makeQuery(id+"F3.opExtrude","SWEPT_BODY",BODY,{"disambiguationData":[OSD([sQuery(id+"F2.wireOp",EDGE,"E2"),sQuery(id+"F2.wireOp",EDGE,"E3"),sQuery(id+"F2.wireOp",EDGE,"E4"),sQuery(id+"F2.wireOp",EDGE,"E5"),sQuery(id+"F2.wireOp",EDGE,"E6"),sQuery(id+"F2.wireOp",EDGE,"E7")])]}),"instanceName":"16"});
            var Q154;
            Q154=makeQuery(id+"F5.opPattern","COPY",BODY,{"derivedFrom":makeQuery(id+"F3.opExtrude","SWEPT_BODY",BODY,{"disambiguationData":[OSD([sQuery(id+"F2.wireOp",EDGE,"E2"),sQuery(id+"F2.wireOp",EDGE,"E3"),sQuery(id+"F2.wireOp",EDGE,"E4"),sQuery(id+"F2.wireOp",EDGE,"E5"),sQuery(id+"F2.wireOp",EDGE,"E6"),sQuery(id+"F2.wireOp",EDGE,"E7")])]}),"instanceName":"18"});
            var Q155;
            Q155=makeQuery(id+"F5.opPattern","COPY",BODY,{"derivedFrom":makeQuery(id+"F3.opExtrude","SWEPT_BODY",BODY,{"disambiguationData":[OSD([sQuery(id+"F2.wireOp",EDGE,"E2"),sQuery(id+"F2.wireOp",EDGE,"E3"),sQuery(id+"F2.wireOp",EDGE,"E4"),sQuery(id+"F2.wireOp",EDGE,"E5"),sQuery(id+"F2.wireOp",EDGE,"E6"),sQuery(id+"F2.wireOp",EDGE,"E7")])]}),"instanceName":"19"});
            var Q156;
            Q156=makeQuery(id+"F5.opPattern","COPY",BODY,{"derivedFrom":makeQuery(id+"F3.opExtrude","SWEPT_BODY",BODY,{"disambiguationData":[OSD([sQuery(id+"F2.wireOp",EDGE,"E2"),sQuery(id+"F2.wireOp",EDGE,"E3"),sQuery(id+"F2.wireOp",EDGE,"E4"),sQuery(id+"F2.wireOp",EDGE,"E5"),sQuery(id+"F2.wireOp",EDGE,"E6"),sQuery(id+"F2.wireOp",EDGE,"E7")])]}),"instanceName":"20"});
            var Q157;
            Q157=makeQuery(id+"F5.opPattern","COPY",BODY,{"derivedFrom":makeQuery(id+"F3.opExtrude","SWEPT_BODY",BODY,{"disambiguationData":[OSD([sQuery(id+"F2.wireOp",EDGE,"E2"),sQuery(id+"F2.wireOp",EDGE,"E3"),sQuery(id+"F2.wireOp",EDGE,"E4"),sQuery(id+"F2.wireOp",EDGE,"E5"),sQuery(id+"F2.wireOp",EDGE,"E6"),sQuery(id+"F2.wireOp",EDGE,"E7")])]}),"instanceName":"22"});
            var Q158;
            Q158=makeQuery(id+"F5.opPattern","COPY",BODY,{"derivedFrom":makeQuery(id+"F3.opExtrude","SWEPT_BODY",BODY,{"disambiguationData":[OSD([sQuery(id+"F2.wireOp",EDGE,"E2"),sQuery(id+"F2.wireOp",EDGE,"E3"),sQuery(id+"F2.wireOp",EDGE,"E4"),sQuery(id+"F2.wireOp",EDGE,"E5"),sQuery(id+"F2.wireOp",EDGE,"E6"),sQuery(id+"F2.wireOp",EDGE,"E7")])]}),"instanceName":"23"});
            var Q159;
            Q159=makeQuery(id+"F5.opPattern","COPY",BODY,{"derivedFrom":makeQuery(id+"F3.opExtrude","SWEPT_BODY",BODY,{"disambiguationData":[OSD([sQuery(id+"F2.wireOp",EDGE,"E2"),sQuery(id+"F2.wireOp",EDGE,"E3"),sQuery(id+"F2.wireOp",EDGE,"E4"),sQuery(id+"F2.wireOp",EDGE,"E5"),sQuery(id+"F2.wireOp",EDGE,"E6"),sQuery(id+"F2.wireOp",EDGE,"E7")])]}),"instanceName":"24"});
            var Q160;
            Q160=makeQuery(id+"F6.opPattern","COPY",BODY,{"derivedFrom":makeQuery(id+"F3.opExtrude","SWEPT_BODY",BODY,{"disambiguationData":[OSD([sQuery(id+"F2.wireOp",EDGE,"E2"),sQuery(id+"F2.wireOp",EDGE,"E3"),sQuery(id+"F2.wireOp",EDGE,"E4"),sQuery(id+"F2.wireOp",EDGE,"E5"),sQuery(id+"F2.wireOp",EDGE,"E6"),sQuery(id+"F2.wireOp",EDGE,"E7")])]}),"instanceName":"1"});
            var Q161;
            Q161=makeQuery(id+"F6.opPattern","COPY",BODY,{"derivedFrom":makeQuery(id+"F4.opPattern","COPY",BODY,{"derivedFrom":makeQuery(id+"F3.opExtrude","SWEPT_BODY",BODY,{"disambiguationData":[OSD([sQuery(id+"F2.wireOp",EDGE,"E2"),sQuery(id+"F2.wireOp",EDGE,"E3"),sQuery(id+"F2.wireOp",EDGE,"E4"),sQuery(id+"F2.wireOp",EDGE,"E5"),sQuery(id+"F2.wireOp",EDGE,"E6"),sQuery(id+"F2.wireOp",EDGE,"E7")])]}),"instanceName":"1"}),"instanceName":"1"});
            var Q162;
            Q162=makeQuery(id+"F6.opPattern","COPY",BODY,{"derivedFrom":makeQuery(id+"F4.opPattern","COPY",BODY,{"derivedFrom":makeQuery(id+"F3.opExtrude","SWEPT_BODY",BODY,{"disambiguationData":[OSD([sQuery(id+"F2.wireOp",EDGE,"E2"),sQuery(id+"F2.wireOp",EDGE,"E3"),sQuery(id+"F2.wireOp",EDGE,"E4"),sQuery(id+"F2.wireOp",EDGE,"E5"),sQuery(id+"F2.wireOp",EDGE,"E6"),sQuery(id+"F2.wireOp",EDGE,"E7")])]}),"instanceName":"3"}),"instanceName":"1"});
            var Q163;
            Q163=makeQuery(id+"F4.opPattern","COPY",BODY,{"derivedFrom":makeQuery(id+"F3.opExtrude","SWEPT_BODY",BODY,{"disambiguationData":[OSD([sQuery(id+"F2.wireOp",EDGE,"E2"),sQuery(id+"F2.wireOp",EDGE,"E3"),sQuery(id+"F2.wireOp",EDGE,"E4"),sQuery(id+"F2.wireOp",EDGE,"E5"),sQuery(id+"F2.wireOp",EDGE,"E6"),sQuery(id+"F2.wireOp",EDGE,"E7")])]}),"instanceName":"4"});
            var Q164;
            Q164=makeQuery(id+"F6.opPattern","COPY",BODY,{"derivedFrom":makeQuery(id+"F5.opPattern","COPY",BODY,{"derivedFrom":makeQuery(id+"F3.opExtrude","SWEPT_BODY",BODY,{"disambiguationData":[OSD([sQuery(id+"F2.wireOp",EDGE,"E2"),sQuery(id+"F2.wireOp",EDGE,"E3"),sQuery(id+"F2.wireOp",EDGE,"E4"),sQuery(id+"F2.wireOp",EDGE,"E5"),sQuery(id+"F2.wireOp",EDGE,"E6"),sQuery(id+"F2.wireOp",EDGE,"E7")])]}),"instanceName":"3"}),"instanceName":"3"});
            var Q165;
            Q165=makeQuery(id+"F6.opPattern","COPY",BODY,{"derivedFrom":makeQuery(id+"F5.opPattern","COPY",BODY,{"derivedFrom":makeQuery(id+"F3.opExtrude","SWEPT_BODY",BODY,{"disambiguationData":[OSD([sQuery(id+"F2.wireOp",EDGE,"E2"),sQuery(id+"F2.wireOp",EDGE,"E3"),sQuery(id+"F2.wireOp",EDGE,"E4"),sQuery(id+"F2.wireOp",EDGE,"E5"),sQuery(id+"F2.wireOp",EDGE,"E6"),sQuery(id+"F2.wireOp",EDGE,"E7")])]}),"instanceName":"2"}),"instanceName":"3"});
            var Q166;
            Q166=makeQuery(id+"F6.opPattern","COPY",BODY,{"derivedFrom":makeQuery(id+"F5.opPattern","COPY",BODY,{"derivedFrom":makeQuery(id+"F3.opExtrude","SWEPT_BODY",BODY,{"disambiguationData":[OSD([sQuery(id+"F2.wireOp",EDGE,"E2"),sQuery(id+"F2.wireOp",EDGE,"E3"),sQuery(id+"F2.wireOp",EDGE,"E4"),sQuery(id+"F2.wireOp",EDGE,"E5"),sQuery(id+"F2.wireOp",EDGE,"E6"),sQuery(id+"F2.wireOp",EDGE,"E7")])]}),"instanceName":"4"}),"instanceName":"3"});
            var Q167;
            Q167=makeQuery(id+"F4.opPattern","COPY",BODY,{"derivedFrom":makeQuery(id+"F3.opExtrude","SWEPT_BODY",BODY,{"disambiguationData":[OSD([sQuery(id+"F2.wireOp",EDGE,"E2"),sQuery(id+"F2.wireOp",EDGE,"E3"),sQuery(id+"F2.wireOp",EDGE,"E4"),sQuery(id+"F2.wireOp",EDGE,"E5"),sQuery(id+"F2.wireOp",EDGE,"E6"),sQuery(id+"F2.wireOp",EDGE,"E7")])]}),"instanceName":"23"});
            var Q168;
            Q168=makeQuery(id+"F4.opPattern","COPY",BODY,{"derivedFrom":makeQuery(id+"F3.opExtrude","SWEPT_BODY",BODY,{"disambiguationData":[OSD([sQuery(id+"F2.wireOp",EDGE,"E2"),sQuery(id+"F2.wireOp",EDGE,"E3"),sQuery(id+"F2.wireOp",EDGE,"E4"),sQuery(id+"F2.wireOp",EDGE,"E5"),sQuery(id+"F2.wireOp",EDGE,"E6"),sQuery(id+"F2.wireOp",EDGE,"E7")])]}),"instanceName":"21"});
            var Q169;
            Q169=makeQuery(id+"F4.opPattern","COPY",BODY,{"derivedFrom":makeQuery(id+"F3.opExtrude","SWEPT_BODY",BODY,{"disambiguationData":[OSD([sQuery(id+"F2.wireOp",EDGE,"E2"),sQuery(id+"F2.wireOp",EDGE,"E3"),sQuery(id+"F2.wireOp",EDGE,"E4"),sQuery(id+"F2.wireOp",EDGE,"E5"),sQuery(id+"F2.wireOp",EDGE,"E6"),sQuery(id+"F2.wireOp",EDGE,"E7")])]}),"instanceName":"24"});
            var Q170;
            Q170=makeQuery(id+"F4.opPattern","COPY",BODY,{"derivedFrom":makeQuery(id+"F3.opExtrude","SWEPT_BODY",BODY,{"disambiguationData":[OSD([sQuery(id+"F2.wireOp",EDGE,"E2"),sQuery(id+"F2.wireOp",EDGE,"E3"),sQuery(id+"F2.wireOp",EDGE,"E4"),sQuery(id+"F2.wireOp",EDGE,"E5"),sQuery(id+"F2.wireOp",EDGE,"E6"),sQuery(id+"F2.wireOp",EDGE,"E7")])]}),"instanceName":"22"});
            var Q171;
            Q171=makeQuery(id+"F4.opPattern","COPY",BODY,{"derivedFrom":makeQuery(id+"F3.opExtrude","SWEPT_BODY",BODY,{"disambiguationData":[OSD([sQuery(id+"F2.wireOp",EDGE,"E2"),sQuery(id+"F2.wireOp",EDGE,"E3"),sQuery(id+"F2.wireOp",EDGE,"E4"),sQuery(id+"F2.wireOp",EDGE,"E5"),sQuery(id+"F2.wireOp",EDGE,"E6"),sQuery(id+"F2.wireOp",EDGE,"E7")])]}),"instanceName":"20"});
            var Q172;
            Q172=makeQuery(id+"F4.opPattern","COPY",BODY,{"derivedFrom":makeQuery(id+"F3.opExtrude","SWEPT_BODY",BODY,{"disambiguationData":[OSD([sQuery(id+"F2.wireOp",EDGE,"E2"),sQuery(id+"F2.wireOp",EDGE,"E3"),sQuery(id+"F2.wireOp",EDGE,"E4"),sQuery(id+"F2.wireOp",EDGE,"E5"),sQuery(id+"F2.wireOp",EDGE,"E6"),sQuery(id+"F2.wireOp",EDGE,"E7")])]}),"instanceName":"19"});
            var Q173;
            Q173=makeQuery(id+"F4.opPattern","COPY",BODY,{"derivedFrom":makeQuery(id+"F3.opExtrude","SWEPT_BODY",BODY,{"disambiguationData":[OSD([sQuery(id+"F2.wireOp",EDGE,"E2"),sQuery(id+"F2.wireOp",EDGE,"E3"),sQuery(id+"F2.wireOp",EDGE,"E4"),sQuery(id+"F2.wireOp",EDGE,"E5"),sQuery(id+"F2.wireOp",EDGE,"E6"),sQuery(id+"F2.wireOp",EDGE,"E7")])]}),"instanceName":"18"});
            var Q174;
            Q174=makeQuery(id+"F4.opPattern","COPY",BODY,{"derivedFrom":makeQuery(id+"F3.opExtrude","SWEPT_BODY",BODY,{"disambiguationData":[OSD([sQuery(id+"F2.wireOp",EDGE,"E2"),sQuery(id+"F2.wireOp",EDGE,"E3"),sQuery(id+"F2.wireOp",EDGE,"E4"),sQuery(id+"F2.wireOp",EDGE,"E5"),sQuery(id+"F2.wireOp",EDGE,"E6"),sQuery(id+"F2.wireOp",EDGE,"E7")])]}),"instanceName":"17"});
            var Q175;
            Q175=makeQuery(id+"F4.opPattern","COPY",BODY,{"derivedFrom":makeQuery(id+"F3.opExtrude","SWEPT_BODY",BODY,{"disambiguationData":[OSD([sQuery(id+"F2.wireOp",EDGE,"E2"),sQuery(id+"F2.wireOp",EDGE,"E3"),sQuery(id+"F2.wireOp",EDGE,"E4"),sQuery(id+"F2.wireOp",EDGE,"E5"),sQuery(id+"F2.wireOp",EDGE,"E6"),sQuery(id+"F2.wireOp",EDGE,"E7")])]}),"instanceName":"16"});
            var Q176;
            Q176=makeQuery(id+"F4.opPattern","COPY",BODY,{"derivedFrom":makeQuery(id+"F3.opExtrude","SWEPT_BODY",BODY,{"disambiguationData":[OSD([sQuery(id+"F2.wireOp",EDGE,"E2"),sQuery(id+"F2.wireOp",EDGE,"E3"),sQuery(id+"F2.wireOp",EDGE,"E4"),sQuery(id+"F2.wireOp",EDGE,"E5"),sQuery(id+"F2.wireOp",EDGE,"E6"),sQuery(id+"F2.wireOp",EDGE,"E7")])]}),"instanceName":"15"});
            var Q177;
            Q177=makeQuery(id+"F4.opPattern","COPY",BODY,{"derivedFrom":makeQuery(id+"F3.opExtrude","SWEPT_BODY",BODY,{"disambiguationData":[OSD([sQuery(id+"F2.wireOp",EDGE,"E2"),sQuery(id+"F2.wireOp",EDGE,"E3"),sQuery(id+"F2.wireOp",EDGE,"E4"),sQuery(id+"F2.wireOp",EDGE,"E5"),sQuery(id+"F2.wireOp",EDGE,"E6"),sQuery(id+"F2.wireOp",EDGE,"E7")])]}),"instanceName":"14"});
            var Q178;
            Q178=makeQuery(id+"F4.opPattern","COPY",BODY,{"derivedFrom":makeQuery(id+"F3.opExtrude","SWEPT_BODY",BODY,{"disambiguationData":[OSD([sQuery(id+"F2.wireOp",EDGE,"E2"),sQuery(id+"F2.wireOp",EDGE,"E3"),sQuery(id+"F2.wireOp",EDGE,"E4"),sQuery(id+"F2.wireOp",EDGE,"E5"),sQuery(id+"F2.wireOp",EDGE,"E6"),sQuery(id+"F2.wireOp",EDGE,"E7")])]}),"instanceName":"13"});
            var Q179;
            Q179=makeQuery(id+"F4.opPattern","COPY",BODY,{"derivedFrom":makeQuery(id+"F3.opExtrude","SWEPT_BODY",BODY,{"disambiguationData":[OSD([sQuery(id+"F2.wireOp",EDGE,"E2"),sQuery(id+"F2.wireOp",EDGE,"E3"),sQuery(id+"F2.wireOp",EDGE,"E4"),sQuery(id+"F2.wireOp",EDGE,"E5"),sQuery(id+"F2.wireOp",EDGE,"E6"),sQuery(id+"F2.wireOp",EDGE,"E7")])]}),"instanceName":"12"});
            var Q180;
            Q180=makeQuery(id+"F4.opPattern","COPY",BODY,{"derivedFrom":makeQuery(id+"F3.opExtrude","SWEPT_BODY",BODY,{"disambiguationData":[OSD([sQuery(id+"F2.wireOp",EDGE,"E2"),sQuery(id+"F2.wireOp",EDGE,"E3"),sQuery(id+"F2.wireOp",EDGE,"E4"),sQuery(id+"F2.wireOp",EDGE,"E5"),sQuery(id+"F2.wireOp",EDGE,"E6"),sQuery(id+"F2.wireOp",EDGE,"E7")])]}),"instanceName":"11"});
            var Q181;
            Q181=makeQuery(id+"F4.opPattern","COPY",BODY,{"derivedFrom":makeQuery(id+"F3.opExtrude","SWEPT_BODY",BODY,{"disambiguationData":[OSD([sQuery(id+"F2.wireOp",EDGE,"E2"),sQuery(id+"F2.wireOp",EDGE,"E3"),sQuery(id+"F2.wireOp",EDGE,"E4"),sQuery(id+"F2.wireOp",EDGE,"E5"),sQuery(id+"F2.wireOp",EDGE,"E6"),sQuery(id+"F2.wireOp",EDGE,"E7")])]}),"instanceName":"10"});
            var Q182;
            Q182=makeQuery(id+"F4.opPattern","COPY",BODY,{"derivedFrom":makeQuery(id+"F3.opExtrude","SWEPT_BODY",BODY,{"disambiguationData":[OSD([sQuery(id+"F2.wireOp",EDGE,"E2"),sQuery(id+"F2.wireOp",EDGE,"E3"),sQuery(id+"F2.wireOp",EDGE,"E4"),sQuery(id+"F2.wireOp",EDGE,"E5"),sQuery(id+"F2.wireOp",EDGE,"E6"),sQuery(id+"F2.wireOp",EDGE,"E7")])]}),"instanceName":"9"});
            var Q183;
            Q183=makeQuery(id+"F4.opPattern","COPY",BODY,{"derivedFrom":makeQuery(id+"F3.opExtrude","SWEPT_BODY",BODY,{"disambiguationData":[OSD([sQuery(id+"F2.wireOp",EDGE,"E2"),sQuery(id+"F2.wireOp",EDGE,"E3"),sQuery(id+"F2.wireOp",EDGE,"E4"),sQuery(id+"F2.wireOp",EDGE,"E5"),sQuery(id+"F2.wireOp",EDGE,"E6"),sQuery(id+"F2.wireOp",EDGE,"E7")])]}),"instanceName":"8"});
            var Q184;
            Q184=makeQuery(id+"F4.opPattern","COPY",BODY,{"derivedFrom":makeQuery(id+"F3.opExtrude","SWEPT_BODY",BODY,{"disambiguationData":[OSD([sQuery(id+"F2.wireOp",EDGE,"E2"),sQuery(id+"F2.wireOp",EDGE,"E3"),sQuery(id+"F2.wireOp",EDGE,"E4"),sQuery(id+"F2.wireOp",EDGE,"E5"),sQuery(id+"F2.wireOp",EDGE,"E6"),sQuery(id+"F2.wireOp",EDGE,"E7")])]}),"instanceName":"7"});
            var Q185;
            Q185=makeQuery(id+"F8.opExtrude","SWEPT_BODY",BODY,{"disambiguationData":[OSD([sQuery(id+"F7.wireOp",EDGE,"E8")])]});
            var Q186;
            Q186=makeQuery(id+"F4.opPattern","COPY",BODY,{"derivedFrom":makeQuery(id+"F3.opExtrude","SWEPT_BODY",BODY,{"disambiguationData":[OSD([sQuery(id+"F2.wireOp",EDGE,"E2"),sQuery(id+"F2.wireOp",EDGE,"E3"),sQuery(id+"F2.wireOp",EDGE,"E4"),sQuery(id+"F2.wireOp",EDGE,"E5"),sQuery(id+"F2.wireOp",EDGE,"E6"),sQuery(id+"F2.wireOp",EDGE,"E7")])]}),"instanceName":"1"});
            var Q187;
            Q187=makeQuery(id+"F5.opPattern","COPY",BODY,{"derivedFrom":makeQuery(id+"F3.opExtrude","SWEPT_BODY",BODY,{"disambiguationData":[OSD([sQuery(id+"F2.wireOp",EDGE,"E2"),sQuery(id+"F2.wireOp",EDGE,"E3"),sQuery(id+"F2.wireOp",EDGE,"E4"),sQuery(id+"F2.wireOp",EDGE,"E5"),sQuery(id+"F2.wireOp",EDGE,"E6"),sQuery(id+"F2.wireOp",EDGE,"E7")])]}),"instanceName":"2"});
            var Q188;
            Q188=makeQuery(id+"F5.opPattern","COPY",BODY,{"derivedFrom":makeQuery(id+"F3.opExtrude","SWEPT_BODY",BODY,{"disambiguationData":[OSD([sQuery(id+"F2.wireOp",EDGE,"E2"),sQuery(id+"F2.wireOp",EDGE,"E3"),sQuery(id+"F2.wireOp",EDGE,"E4"),sQuery(id+"F2.wireOp",EDGE,"E5"),sQuery(id+"F2.wireOp",EDGE,"E6"),sQuery(id+"F2.wireOp",EDGE,"E7")])]}),"instanceName":"3"});
            var Q189;
            Q189=makeQuery(id+"F5.opPattern","COPY",BODY,{"derivedFrom":makeQuery(id+"F3.opExtrude","SWEPT_BODY",BODY,{"disambiguationData":[OSD([sQuery(id+"F2.wireOp",EDGE,"E2"),sQuery(id+"F2.wireOp",EDGE,"E3"),sQuery(id+"F2.wireOp",EDGE,"E4"),sQuery(id+"F2.wireOp",EDGE,"E5"),sQuery(id+"F2.wireOp",EDGE,"E6"),sQuery(id+"F2.wireOp",EDGE,"E7")])]}),"instanceName":"5"});
            var Q190;
            Q190=makeQuery(id+"F5.opPattern","COPY",BODY,{"derivedFrom":makeQuery(id+"F3.opExtrude","SWEPT_BODY",BODY,{"disambiguationData":[OSD([sQuery(id+"F2.wireOp",EDGE,"E2"),sQuery(id+"F2.wireOp",EDGE,"E3"),sQuery(id+"F2.wireOp",EDGE,"E4"),sQuery(id+"F2.wireOp",EDGE,"E5"),sQuery(id+"F2.wireOp",EDGE,"E6"),sQuery(id+"F2.wireOp",EDGE,"E7")])]}),"instanceName":"6"});
            var Q191;
            Q191=makeQuery(id+"F5.opPattern","COPY",BODY,{"derivedFrom":makeQuery(id+"F3.opExtrude","SWEPT_BODY",BODY,{"disambiguationData":[OSD([sQuery(id+"F2.wireOp",EDGE,"E2"),sQuery(id+"F2.wireOp",EDGE,"E3"),sQuery(id+"F2.wireOp",EDGE,"E4"),sQuery(id+"F2.wireOp",EDGE,"E5"),sQuery(id+"F2.wireOp",EDGE,"E6"),sQuery(id+"F2.wireOp",EDGE,"E7")])]}),"instanceName":"7"});
            var Q192;
            Q192=makeQuery(id+"F6.opPattern","COPY",BODY,{"derivedFrom":makeQuery(id+"F4.opPattern","COPY",BODY,{"derivedFrom":makeQuery(id+"F3.opExtrude","SWEPT_BODY",BODY,{"disambiguationData":[OSD([sQuery(id+"F2.wireOp",EDGE,"E2"),sQuery(id+"F2.wireOp",EDGE,"E3"),sQuery(id+"F2.wireOp",EDGE,"E4"),sQuery(id+"F2.wireOp",EDGE,"E5"),sQuery(id+"F2.wireOp",EDGE,"E6"),sQuery(id+"F2.wireOp",EDGE,"E7")])]}),"instanceName":"24"}),"instanceName":"3"});
            var Q193;
            Q193=makeQuery(id+"F6.opPattern","COPY",BODY,{"derivedFrom":makeQuery(id+"F5.opPattern","COPY",BODY,{"derivedFrom":makeQuery(id+"F3.opExtrude","SWEPT_BODY",BODY,{"disambiguationData":[OSD([sQuery(id+"F2.wireOp",EDGE,"E2"),sQuery(id+"F2.wireOp",EDGE,"E3"),sQuery(id+"F2.wireOp",EDGE,"E4"),sQuery(id+"F2.wireOp",EDGE,"E5"),sQuery(id+"F2.wireOp",EDGE,"E6"),sQuery(id+"F2.wireOp",EDGE,"E7")])]}),"instanceName":"24"}),"instanceName":"3"});
            var Q194;
            Q194=makeQuery(id+"F8.opExtrude","SWEPT_BODY",BODY,{"disambiguationData":[OSD([sQuery(id+"F7.wireOp",EDGE,"E9.3.0")])]});
            var Q195;
            Q195=makeQuery(id+"F8.opExtrude","SWEPT_BODY",BODY,{"disambiguationData":[OSD([sQuery(id+"F7.wireOp",EDGE,"E9.2.0")])]});
            var Q196;
            Q196=makeQuery(id+"F8.opExtrude","SWEPT_BODY",BODY,{"disambiguationData":[OSD([sQuery(id+"F7.wireOp",EDGE,"E9.1.0")])]});
            var Q197;
            Q197=makeQuery(id+"F4.opPattern","COPY",BODY,{"derivedFrom":makeQuery(id+"F3.opExtrude","SWEPT_BODY",BODY,{"disambiguationData":[OSD([sQuery(id+"F2.wireOp",EDGE,"E2"),sQuery(id+"F2.wireOp",EDGE,"E3"),sQuery(id+"F2.wireOp",EDGE,"E4"),sQuery(id+"F2.wireOp",EDGE,"E5"),sQuery(id+"F2.wireOp",EDGE,"E6"),sQuery(id+"F2.wireOp",EDGE,"E7")])]}),"instanceName":"3"});
            var Q198;
            Q198=makeQuery(id+"F4.opPattern","COPY",BODY,{"derivedFrom":makeQuery(id+"F3.opExtrude","SWEPT_BODY",BODY,{"disambiguationData":[OSD([sQuery(id+"F2.wireOp",EDGE,"E2"),sQuery(id+"F2.wireOp",EDGE,"E3"),sQuery(id+"F2.wireOp",EDGE,"E4"),sQuery(id+"F2.wireOp",EDGE,"E5"),sQuery(id+"F2.wireOp",EDGE,"E6"),sQuery(id+"F2.wireOp",EDGE,"E7")])]}),"instanceName":"2"});
            var Q199;
            Q199=makeQuery(id+"F3.opExtrude","SWEPT_BODY",BODY,{"disambiguationData":[OSD([sQuery(id+"F2.wireOp",EDGE,"E2"),sQuery(id+"F2.wireOp",EDGE,"E3"),sQuery(id+"F2.wireOp",EDGE,"E4"),sQuery(id+"F2.wireOp",EDGE,"E5"),sQuery(id+"F2.wireOp",EDGE,"E6"),sQuery(id+"F2.wireOp",EDGE,"E7")])]});
            var Q200;
            Q200=makeQuery(id+"F1.opExtrude","SWEPT_BODY",BODY,{"disambiguationData":[OSD([sQuery(id+"F0.wireOp",EDGE,"E0"),sQuery(id+"F0.wireOp",EDGE,"E1")])]});
            booleanBodies(context, id + "F9", {"operationType" : BooleanOperationType.SUBTRACTION, "tools" : qUnion([Q0, Q1, Q2, Q3, Q4, Q5, Q6, Q7, Q8, Q9, Q10, Q11, Q12, Q13, Q14, Q15, Q16, Q17, Q18, Q19, Q20, Q21, Q22, Q23, Q24, Q25, Q26, Q27, Q28, Q29, Q30, Q31, Q32, Q33, Q34, Q35, Q36, Q37, Q38, Q39, Q40, Q41, Q42, Q43, Q44, Q45, Q46, Q47, Q48, Q49, Q50, Q51, Q52, Q53, Q54, Q55, Q56, Q57, Q58, Q59, Q60, Q61, Q62, Q63, Q64, Q65, Q66, Q67, Q68, Q69, Q70, Q71, Q72, Q73, Q74, Q75, Q76, Q77, Q78, Q79, Q80, Q81, Q82, Q83, Q84, Q85, Q86, Q87, Q88, Q89, Q90, Q91, Q92, Q93, Q94, Q95, Q96, Q97, Q98, Q99, Q100, Q101, Q102, Q103, Q104, Q105, Q106, Q107, Q108, Q109, Q110, Q111, Q112, Q113, Q114, Q115, Q116, Q117, Q118, Q119, Q120, Q121, Q122, Q123, Q124, Q125, Q126, Q127, Q128, Q129, Q130, Q131, Q132, Q133, Q134, Q135, Q136, Q137, Q138, Q139, Q140, Q141, Q142, Q143, Q144, Q145, Q146, Q147, Q148, Q149, Q150, Q151, Q152, Q153, Q154, Q155, Q156, Q157, Q158, Q159, Q160, Q161, Q162, Q163, Q164, Q165, Q166, Q167, Q168, Q169, Q170, Q171, Q172, Q173, Q174, Q175, Q176, Q177, Q178, Q179, Q180, Q181, Q182, Q183, Q184, Q185, Q186, Q187, Q188, Q189, Q190, Q191, Q192, Q193, Q194, Q195, Q196, Q197, Q198, Q199]), "targets" : qUnion([Q200])});
        }
        {
            var Q0;
            Q0=makeQuery(id+"F1.opExtrude","SWEPT_BODY",BODY,{"disambiguationData":[OSD([sQuery(id+"F0.wireOp",EDGE,"E0"),sQuery(id+"F0.wireOp",EDGE,"E1")])]});
            var Q1;
            Q1=sQuery(id+"F0.wireOp",VERTEX,"E0.center");
            transform(context, id + "F10", {"entities" : qUnion([Q0]), "transformType" : TransformType.SCALE_UNIFORMLY, "scale" : 2.6, "scalePoint" : qUnion([Q1]), "makeCopy" : false});
        }
    });
